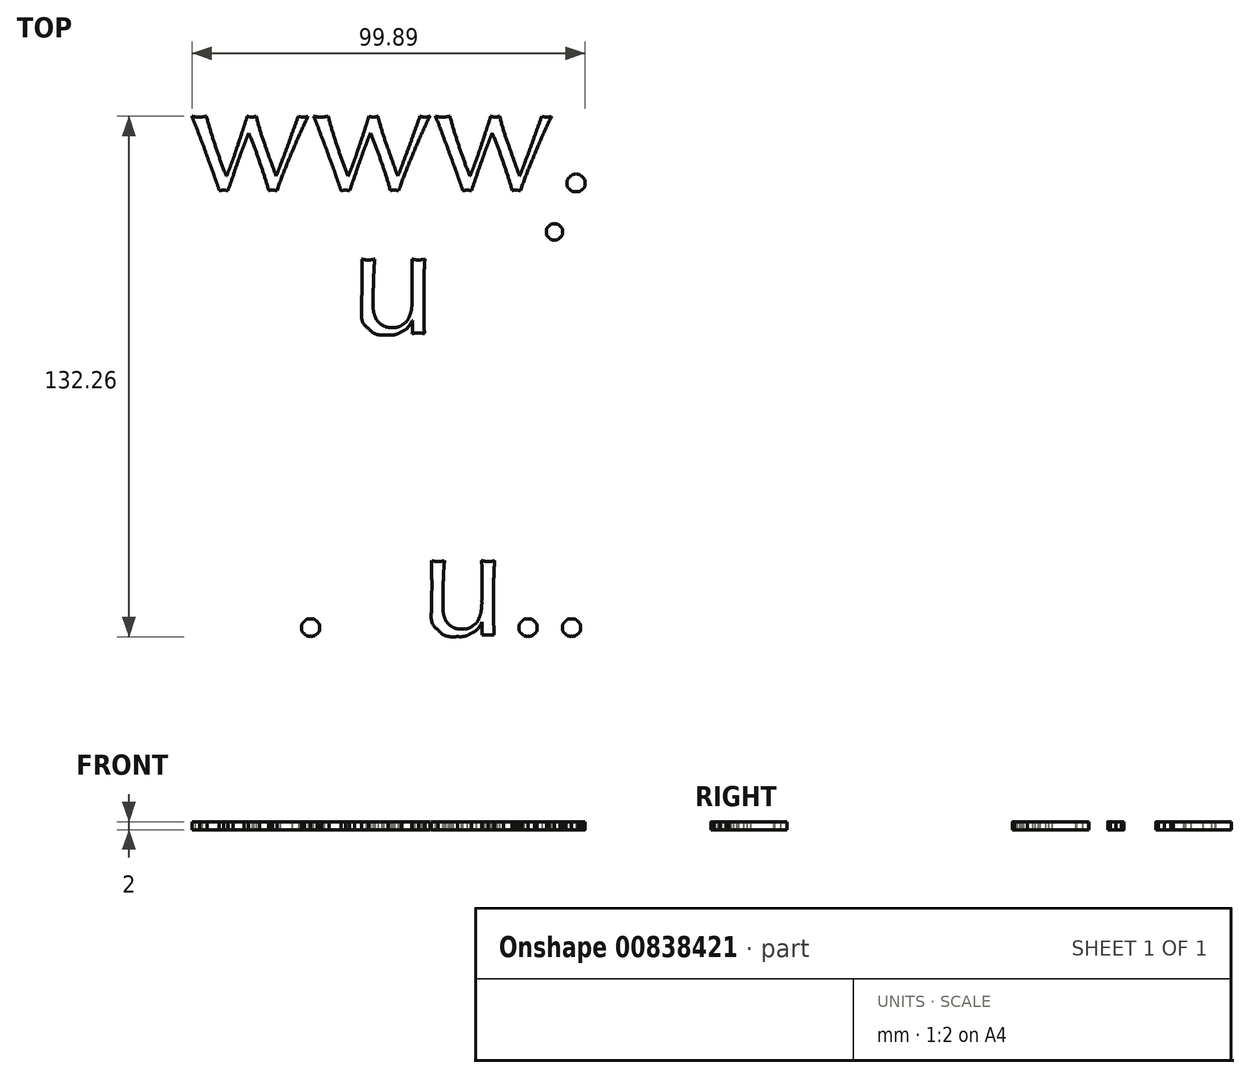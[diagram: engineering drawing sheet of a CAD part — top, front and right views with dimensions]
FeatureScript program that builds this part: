
annotation { "Feature Type Name" : "Feature", "Feature Type Description" : "" }
export const myFeature = defineFeature(function(context is Context, id is Id, definition is map)
    precondition{}
    {
        {
            var Q0;
            Q0=qCreatedBy(makeId("Top.planeOp"),FACE);
            var sketch = newSketch(context, id + "F0", { "sketchPlane" : qUnion([Q0])});
            skLineSegment(sketch, "E0", {"start": v(54.7, 60.68) * mm, "end": v(54.7, 58.25) * mm});
            skLineSegment(sketch, "E1", {"start": v(54.7, 58.25) * mm, "end": v(54.7, 60.68) * mm});
            skLineSegment(sketch, "E2", {"start": v(57.65, 51.93) * mm, "end": v(57.65, 54.51) * mm});
            skLineSegment(sketch, "E3", {"start": v(57.65, 54.51) * mm, "end": v(57.65, 51.93) * mm});
            skLineSegment(sketch, "E4", {"start": v(45.08, 65.22) * mm, "end": v(45, 65.22) * mm});
            skLineSegment(sketch, "E5", {"start": v(45, 65.22) * mm, "end": v(45.08, 65.22) * mm});
            skLineSegment(sketch, "E6", {"start": v(42.06, 60.96) * mm, "end": v(42.06, 56.82) * mm});
            skLineSegment(sketch, "E7", {"start": v(42.06, 56.82) * mm, "end": v(42.06, 60.96) * mm});
            skLineSegment(sketch, "E8", {"start": v(45, 56.82) * mm, "end": v(45, 60.2) * mm});
            skLineSegment(sketch, "E9", {"start": v(45, 60.2) * mm, "end": v(45, 56.82) * mm});
            skLineSegment(sketch, "E10", {"start": v(-41.95, 23.11) * mm, "end": v(-42.11, 17.14) * mm});
            skLineSegment(sketch, "E11", {"start": v(-42.11, 17.14) * mm, "end": v(-41.95, 23.11) * mm});
            skLineSegment(sketch, "E12", {"start": v(-51.78, 30.2) * mm, "end": v(-51.78, 28.12) * mm});
            skLineSegment(sketch, "E13", {"start": v(-51.78, 28.12) * mm, "end": v(-51.34, 28.12) * mm});
            skLineSegment(sketch, "E14", {"start": v(-51.34, 28.12) * mm, "end": v(-51.78, 30.2) * mm});
            skLineSegment(sketch, "E15", {"start": v(-36.7, 13.68) * mm, "end": v(-36.7, 14.56) * mm});
            skLineSegment(sketch, "E16", {"start": v(-36.7, 14.56) * mm, "end": v(-36.7, 13.68) * mm});
            skLineSegment(sketch, "E17", {"start": v(-28.94, 37.43) * mm, "end": v(-32.24, 36.04) * mm});
            skLineSegment(sketch, "E18", {"start": v(-32.24, 36.04) * mm, "end": v(-28.94, 37.43) * mm});
            skLineSegment(sketch, "E19", {"start": v(-33.28, 30.07) * mm, "end": v(-32, 30.07) * mm});
            skLineSegment(sketch, "E20", {"start": v(-32, 30.07) * mm, "end": v(-33.28, 30.07) * mm});
            skLineSegment(sketch, "E21", {"start": v(-24.33, 13.28) * mm, "end": v(-24.33, 14.24) * mm});
            skLineSegment(sketch, "E22", {"start": v(-24.33, 14.24) * mm, "end": v(-24.33, 13.28) * mm});
            skLineSegment(sketch, "E23", {"start": v(-29.06, 30.07) * mm, "end": v(-27.11, 30.07) * mm});
            skLineSegment(sketch, "E24", {"start": v(-27.11, 30.07) * mm, "end": v(-29.06, 30.07) * mm});
            skLineSegment(sketch, "E25", {"start": v(-24.88, 30.4) * mm, "end": v(-24.88, 30.83) * mm});
            skLineSegment(sketch, "E26", {"start": v(-24.88, 30.83) * mm, "end": v(-24.88, 31.23) * mm});
            skLineSegment(sketch, "E27", {"start": v(-24.88, 31.23) * mm, "end": v(-24.88, 30.4) * mm});
            skLineSegment(sketch, "E28", {"start": v(-28.74, 37.43) * mm, "end": v(-28.94, 37.43) * mm});
            skLineSegment(sketch, "E29", {"start": v(-28.94, 37.43) * mm, "end": v(-28.74, 37.43) * mm});
            skLineSegment(sketch, "E30", {"start": v(-8.4, 16.5) * mm, "end": v(-8.32, 16.5) * mm});
            skLineSegment(sketch, "E31", {"start": v(-8.32, 16.5) * mm, "end": v(-8.32, 14.8) * mm});
            skLineSegment(sketch, "E32", {"start": v(-8.32, 14.8) * mm, "end": v(-8.4, 16.5) * mm});
            skLineSegment(sketch, "E33", {"start": v(-8.4, 28.92) * mm, "end": v(-8.4, 25.58) * mm});
            skLineSegment(sketch, "E34", {"start": v(-8.4, 25.58) * mm, "end": v(-8.4, 28.92) * mm});
            skLineSegment(sketch, "E35", {"start": v(9.93, 28.84) * mm, "end": v(10.2, 29.04) * mm});
            skLineSegment(sketch, "E36", {"start": v(10.2, 29.04) * mm, "end": v(9.93, 28.84) * mm});
            skLineSegment(sketch, "E37", {"start": v(3.96, 28.2) * mm, "end": v(3.88, 28.24) * mm});
            skLineSegment(sketch, "E38", {"start": v(3.88, 28.24) * mm, "end": v(3.96, 28.2) * mm});
            skLineSegment(sketch, "E39", {"start": v(0.98, 23.87) * mm, "end": v(0.98, 22.6) * mm});
            skLineSegment(sketch, "E40", {"start": v(0.98, 22.6) * mm, "end": v(0.98, 23.87) * mm});
            skLineSegment(sketch, "E41", {"start": v(3.92, 19.57) * mm, "end": v(3.92, 23.95) * mm});
            skLineSegment(sketch, "E42", {"start": v(3.92, 23.95) * mm, "end": v(3.92, 19.57) * mm});
            skLineSegment(sketch, "E43", {"start": v(15.14, 31.74) * mm, "end": v(15.14, 24.54) * mm});
            skLineSegment(sketch, "E44", {"start": v(15.14, 24.54) * mm, "end": v(15.14, 31.74) * mm});
            skLineSegment(sketch, "E45", {"start": v(18.09, 24.54) * mm, "end": v(18.09, 31.74) * mm});
            skLineSegment(sketch, "E46", {"start": v(18.09, 31.74) * mm, "end": v(18.09, 24.54) * mm});
            skLineSegment(sketch, "E47", {"start": v(26.26, 24.66) * mm, "end": v(26.26, 20.52) * mm});
            skLineSegment(sketch, "E48", {"start": v(26.26, 20.52) * mm, "end": v(26.26, 24.66) * mm});
            skLineSegment(sketch, "E49", {"start": v(29.2, 20.52) * mm, "end": v(29.2, 24.66) * mm});
            skLineSegment(sketch, "E50", {"start": v(29.2, 24.66) * mm, "end": v(29.2, 20.52) * mm});
            skLineSegment(sketch, "E51", {"start": v(39.12, 20.13) * mm, "end": v(39.12, 20.05) * mm});
            skLineSegment(sketch, "E52", {"start": v(39.12, 20.05) * mm, "end": v(39.12, 20.13) * mm});
            skLineSegment(sketch, "E53", {"start": v(38.8, 13.56) * mm, "end": v(38.8, 13.48) * mm});
            skLineSegment(sketch, "E54", {"start": v(38.8, 13.48) * mm, "end": v(38.8, 13.56) * mm});
            skLineSegment(sketch, "E55", {"start": v(47.56, 30.95) * mm, "end": v(47.64, 31.03) * mm});
            skLineSegment(sketch, "E56", {"start": v(47.64, 31.03) * mm, "end": v(47.56, 30.95) * mm});
            skLineSegment(sketch, "E57", {"start": v(-44.7, -11.51) * mm, "end": v(-44.79, -11.51) * mm});
            skLineSegment(sketch, "E58", {"start": v(-44.79, -11.51) * mm, "end": v(-44.7, -11.51) * mm});
            skLineSegment(sketch, "E59", {"start": v(-47.73, -8.13) * mm, "end": v(-47.73, -15.33) * mm});
            skLineSegment(sketch, "E60", {"start": v(-47.73, -15.33) * mm, "end": v(-47.73, -8.13) * mm});
            skLineSegment(sketch, "E61", {"start": v(-48.05, -26.6) * mm, "end": v(-47.33, -26.6) * mm});
            skLineSegment(sketch, "E62", {"start": v(-47.33, -26.6) * mm, "end": v(-48.05, -26.6) * mm});
            skLineSegment(sketch, "E63", {"start": v(-14.92, -16.77) * mm, "end": v(-15.08, -22.73) * mm});
            skLineSegment(sketch, "E64", {"start": v(-15.08, -22.73) * mm, "end": v(-14.92, -16.77) * mm});
            skLineSegment(sketch, "E65", {"start": v(-24.75, -9.68) * mm, "end": v(-24.75, -11.75) * mm});
            skLineSegment(sketch, "E66", {"start": v(-24.75, -11.75) * mm, "end": v(-24.31, -11.75) * mm});
            skLineSegment(sketch, "E67", {"start": v(-24.31, -11.75) * mm, "end": v(-24.75, -9.68) * mm});
            skLineSegment(sketch, "E68", {"start": v(-9.67, -26.2) * mm, "end": v(-9.67, -25.32) * mm});
            skLineSegment(sketch, "E69", {"start": v(-9.67, -25.32) * mm, "end": v(-9.67, -26.2) * mm});
            skLineSegment(sketch, "E70", {"start": v(-4.3, -8.13) * mm, "end": v(-4.3, -15.33) * mm});
            skLineSegment(sketch, "E71", {"start": v(-4.3, -15.33) * mm, "end": v(-4.3, -8.13) * mm});
            skLineSegment(sketch, "E72", {"start": v(-1.35, -15.33) * mm, "end": v(-1.35, -8.13) * mm});
            skLineSegment(sketch, "E73", {"start": v(-1.35, -8.13) * mm, "end": v(-1.35, -15.33) * mm});
            skLineSegment(sketch, "E74", {"start": v(16, -16.77) * mm, "end": v(15.85, -22.73) * mm});
            skLineSegment(sketch, "E75", {"start": v(15.85, -22.73) * mm, "end": v(16, -16.77) * mm});
            skLineSegment(sketch, "E76", {"start": v(6.18, -9.68) * mm, "end": v(6.18, -11.75) * mm});
            skLineSegment(sketch, "E77", {"start": v(6.18, -11.75) * mm, "end": v(6.62, -11.75) * mm});
            skLineSegment(sketch, "E78", {"start": v(6.62, -11.75) * mm, "end": v(6.18, -9.68) * mm});
            skLineSegment(sketch, "E79", {"start": v(21.26, -26.2) * mm, "end": v(21.26, -25.32) * mm});
            skLineSegment(sketch, "E80", {"start": v(21.26, -25.32) * mm, "end": v(21.26, -26.2) * mm});
            skLineSegment(sketch, "E81", {"start": v(38.57, -15.5) * mm, "end": v(38.57, -17.92) * mm});
            skLineSegment(sketch, "E82", {"start": v(38.57, -17.92) * mm, "end": v(38.57, -15.5) * mm});
            skLineSegment(sketch, "E83", {"start": v(41.51, -24.25) * mm, "end": v(41.51, -21.66) * mm});
            skLineSegment(sketch, "E84", {"start": v(41.51, -21.66) * mm, "end": v(41.51, -24.25) * mm});
            skLineSegment(sketch, "E85", {"start": v(28.94, -10.96) * mm, "end": v(28.86, -10.96) * mm});
            skLineSegment(sketch, "E86", {"start": v(28.86, -10.96) * mm, "end": v(28.94, -10.96) * mm});
            skLineSegment(sketch, "E87", {"start": v(25.92, -15.21) * mm, "end": v(25.92, -19.35) * mm});
            skLineSegment(sketch, "E88", {"start": v(25.92, -19.35) * mm, "end": v(25.92, -15.21) * mm});
            skLineSegment(sketch, "E89", {"start": v(28.86, -19.35) * mm, "end": v(28.86, -15.97) * mm});
            skLineSegment(sketch, "E90", {"start": v(28.86, -15.97) * mm, "end": v(28.86, -19.35) * mm});
            skLineSegment(sketch, "E91", {"start": v(-52.39, -59.72) * mm, "end": v(-52.86, -59.72) * mm});
            skLineSegment(sketch, "E92", {"start": v(-52.86, -59.72) * mm, "end": v(-52.39, -59.72) * mm});
            skLineSegment(sketch, "E93", {"start": v(-43.83, -48.06) * mm, "end": v(-43.35, -48.06) * mm});
            skLineSegment(sketch, "E94", {"start": v(-43.35, -48.06) * mm, "end": v(-43.83, -48.06) * mm});
            skLineSegment(sketch, "E95", {"start": v(-12.72, -52.24) * mm, "end": v(-12.72, -54.67) * mm});
            skLineSegment(sketch, "E96", {"start": v(-12.72, -54.67) * mm, "end": v(-12.72, -52.24) * mm});
            skLineSegment(sketch, "E97", {"start": v(-9.77, -61) * mm, "end": v(-9.77, -58.4) * mm});
            skLineSegment(sketch, "E98", {"start": v(-9.77, -58.4) * mm, "end": v(-9.77, -61) * mm});
            skLineSegment(sketch, "E99", {"start": v(-22.35, -47.7) * mm, "end": v(-22.42, -47.7) * mm});
            skLineSegment(sketch, "E100", {"start": v(-22.42, -47.7) * mm, "end": v(-22.35, -47.7) * mm});
            skLineSegment(sketch, "E101", {"start": v(-25.37, -51.96) * mm, "end": v(-25.37, -56.1) * mm});
            skLineSegment(sketch, "E102", {"start": v(-25.37, -56.1) * mm, "end": v(-25.37, -51.96) * mm});
            skLineSegment(sketch, "E103", {"start": v(-22.42, -56.1) * mm, "end": v(-22.42, -52.72) * mm});
            skLineSegment(sketch, "E104", {"start": v(-22.42, -52.72) * mm, "end": v(-22.42, -56.1) * mm});
            skLineSegment(sketch, "E105", {"start": v(9.31, -60.12) * mm, "end": v(9.4, -60.12) * mm});
            skLineSegment(sketch, "E106", {"start": v(9.4, -60.12) * mm, "end": v(9.4, -61.83) * mm});
            skLineSegment(sketch, "E107", {"start": v(9.4, -61.83) * mm, "end": v(9.31, -60.12) * mm});
            skLineSegment(sketch, "E108", {"start": v(9.31, -47.7) * mm, "end": v(9.31, -51.05) * mm});
            skLineSegment(sketch, "E109", {"start": v(9.31, -51.05) * mm, "end": v(9.31, -47.7) * mm});
            skLineSegment(sketch, "E110", {"start": v(41.63, -44.88) * mm, "end": v(41.63, -52.08) * mm});
            skLineSegment(sketch, "E111", {"start": v(41.63, -52.08) * mm, "end": v(41.63, -44.88) * mm});
            skLineSegment(sketch, "E112", {"start": v(44.58, -52.08) * mm, "end": v(44.58, -44.88) * mm});
            skLineSegment(sketch, "E113", {"start": v(44.58, -44.88) * mm, "end": v(44.58, -52.08) * mm});
            skLineSegment(sketch, "E114", {"start": v(52.75, -44.88) * mm, "end": v(52.75, -52.08) * mm});
            skLineSegment(sketch, "E115", {"start": v(52.75, -52.08) * mm, "end": v(52.75, -44.88) * mm});
            skLineSegment(sketch, "E116", {"start": v(55.7, -52.08) * mm, "end": v(55.7, -44.88) * mm});
            skLineSegment(sketch, "E117", {"start": v(55.7, -44.88) * mm, "end": v(55.7, -52.08) * mm});
            skFitSpline(sketch, "E118", {"points": [v(-57.43, 49.5) * mm, v(-57.1, 49.55) * mm, v(-56.74, 49.58) * mm, v(-56.31, 49.58) * mm]});
            skFitSpline(sketch, "E119", {"points": [v(-56.31, 49.58) * mm, v(-55.89, 49.58) * mm, v(-55.52, 49.55) * mm, v(-55.2, 49.5) * mm]});
            skFitSpline(sketch, "E120", {"points": [v(-55.2, 49.5) * mm, v(-54.83, 50.62) * mm, v(-54.4, 51.86) * mm, v(-53.93, 53.24) * mm]});
            skFitSpline(sketch, "E121", {"points": [v(-53.93, 53.24) * mm, v(-53.45, 54.65) * mm, v(-52.97, 56.03) * mm, v(-52.5, 57.38) * mm]});
            skFitSpline(sketch, "E122", {"points": [v(-52.5, 57.38) * mm, v(-52.02, 58.73) * mm, v(-51.55, 60) * mm, v(-51.1, 61.16) * mm]});
            skFitSpline(sketch, "E123", {"points": [v(-51.1, 61.16) * mm, v(-50.65, 62.35) * mm, v(-50.27, 63.35) * mm, v(-49.95, 64.14) * mm]});
            skFitSpline(sketch, "E124", {"points": [v(-49.95, 64.14) * mm, v(-48.89, 61.52) * mm, v(-47.94, 59.01) * mm, v(-47.12, 56.62) * mm]});
            skFitSpline(sketch, "E125", {"points": [v(-47.12, 56.62) * mm, v(-46.3, 54.24) * mm, v(-45.54, 51.86) * mm, v(-44.85, 49.5) * mm]});
            skFitSpline(sketch, "E126", {"points": [v(-44.85, 49.5) * mm, v(-44.72, 49.55) * mm, v(-44.56, 49.58) * mm, v(-44.38, 49.58) * mm]});
            skFitSpline(sketch, "E127", {"points": [v(-44.38, 49.58) * mm, v(-44.2, 49.58) * mm, v(-44, 49.58) * mm, v(-43.82, 49.58) * mm]});
            skFitSpline(sketch, "E128", {"points": [v(-43.82, 49.58) * mm, v(-43.42, 49.58) * mm, v(-43.08, 49.55) * mm, v(-42.79, 49.5) * mm]});
            skFitSpline(sketch, "E129", {"points": [v(-42.79, 49.5) * mm, v(-41.64, 52.63) * mm, v(-40.42, 55.76) * mm, v(-39.12, 58.9) * mm]});
            skFitSpline(sketch, "E130", {"points": [v(-39.12, 58.9) * mm, v(-37.8, 62.02) * mm, v(-36.38, 65.2) * mm, v(-34.87, 68.4) * mm]});
            skFitSpline(sketch, "E131", {"points": [v(-34.87, 68.4) * mm, v(-35.32, 68.27) * mm, v(-35.72, 68.2) * mm, v(-36.06, 68.2) * mm]});
            skFitSpline(sketch, "E132", {"points": [v(-36.06, 68.2) * mm, v(-36.38, 68.2) * mm, v(-36.8, 68.27) * mm, v(-37.33, 68.4) * mm]});
            skFitSpline(sketch, "E133", {"points": [v(-37.33, 68.4) * mm, v(-37.79, 67.15) * mm, v(-38.28, 65.81) * mm, v(-38.8, 64.38) * mm]});
            skFitSpline(sketch, "E134", {"points": [v(-38.8, 64.38) * mm, v(-39.31, 62.95) * mm, v(-39.81, 61.54) * mm, v(-40.32, 60.16) * mm]});
            skFitSpline(sketch, "E135", {"points": [v(-40.32, 60.16) * mm, v(-40.82, 58.81) * mm, v(-41.31, 57.51) * mm, v(-41.8, 56.27) * mm]});
            skFitSpline(sketch, "E136", {"points": [v(-41.8, 56.27) * mm, v(-42.24, 55.05) * mm, v(-42.64, 54.01) * mm, v(-42.98, 53.16) * mm]});
            skFitSpline(sketch, "E137", {"points": [v(-42.98, 53.16) * mm, v(-43.94, 55.81) * mm, v(-44.85, 58.37) * mm, v(-45.73, 60.84) * mm]});
            skFitSpline(sketch, "E138", {"points": [v(-45.73, 60.84) * mm, v(-46.6, 63.33) * mm, v(-47.37, 65.85) * mm, v(-48.04, 68.4) * mm]});
            skFitSpline(sketch, "E139", {"points": [v(-48.04, 68.4) * mm, v(-48.25, 68.35) * mm, v(-48.43, 68.3) * mm, v(-48.6, 68.24) * mm]});
            skFitSpline(sketch, "E140", {"points": [v(-48.6, 68.24) * mm, v(-48.75, 68.22) * mm, v(-48.94, 68.2) * mm, v(-49.15, 68.2) * mm]});
            skFitSpline(sketch, "E141", {"points": [v(-49.15, 68.2) * mm, v(-49.47, 68.2) * mm, v(-49.87, 68.27) * mm, v(-50.34, 68.4) * mm]});
            skFitSpline(sketch, "E142", {"points": [v(-50.34, 68.4) * mm, v(-50.72, 67.15) * mm, v(-51.14, 65.8) * mm, v(-51.62, 64.34) * mm]});
            skFitSpline(sketch, "E143", {"points": [v(-51.62, 64.34) * mm, v(-52.1, 62.88) * mm, v(-52.57, 61.45) * mm, v(-53.05, 60.05) * mm]});
            skFitSpline(sketch, "E144", {"points": [v(-53.05, 60.05) * mm, v(-53.53, 58.64) * mm, v(-54, 57.33) * mm, v(-54.44, 56.1) * mm]});
            skFitSpline(sketch, "E145", {"points": [v(-54.44, 56.1) * mm, v(-54.9, 54.89) * mm, v(-55.28, 53.9) * mm, v(-55.6, 53.16) * mm]});
            skFitSpline(sketch, "E146", {"points": [v(-55.6, 53.16) * mm, v(-56.63, 55.81) * mm, v(-57.57, 58.39) * mm, v(-58.42, 60.88) * mm]});
            skFitSpline(sketch, "E147", {"points": [v(-58.42, 60.88) * mm, v(-59.24, 63.4) * mm, v(-60, 65.9) * mm, v(-60.69, 68.4) * mm]});
            skFitSpline(sketch, "E148", {"points": [v(-60.69, 68.4) * mm, v(-61.03, 68.35) * mm, v(-61.35, 68.3) * mm, v(-61.64, 68.24) * mm]});
            skFitSpline(sketch, "E149", {"points": [v(-61.64, 68.24) * mm, v(-61.94, 68.22) * mm, v(-62.23, 68.2) * mm, v(-62.52, 68.2) * mm]});
            skFitSpline(sketch, "E150", {"points": [v(-62.52, 68.2) * mm, v(-62.84, 68.2) * mm, v(-63.16, 68.22) * mm, v(-63.47, 68.24) * mm]});
            skFitSpline(sketch, "E151", {"points": [v(-63.47, 68.24) * mm, v(-63.77, 68.3) * mm, v(-64.07, 68.35) * mm, v(-64.39, 68.4) * mm]});
            skFitSpline(sketch, "E152", {"points": [v(-64.39, 68.4) * mm, v(-63.73, 66.8) * mm, v(-63.06, 65.11) * mm, v(-62.4, 63.3) * mm]});
            skFitSpline(sketch, "E153", {"points": [v(-62.4, 63.3) * mm, v(-61.71, 61.53) * mm, v(-61.06, 59.78) * mm, v(-60.45, 58.06) * mm]});
            skFitSpline(sketch, "E154", {"points": [v(-60.45, 58.06) * mm, v(-59.81, 56.36) * mm, v(-59.23, 54.75) * mm, v(-58.7, 53.24) * mm]});
            skFitSpline(sketch, "E155", {"points": [v(-58.7, 53.24) * mm, v(-58.17, 51.73) * mm, v(-57.75, 50.48) * mm, v(-57.43, 49.5) * mm]});
            skFitSpline(sketch, "E156", {"points": [v(-26.5, 49.5) * mm, v(-26.18, 49.55) * mm, v(-25.8, 49.58) * mm, v(-25.38, 49.58) * mm]});
            skFitSpline(sketch, "E157", {"points": [v(-25.38, 49.58) * mm, v(-24.96, 49.58) * mm, v(-24.59, 49.55) * mm, v(-24.27, 49.5) * mm]});
            skFitSpline(sketch, "E158", {"points": [v(-24.27, 49.5) * mm, v(-23.9, 50.62) * mm, v(-23.47, 51.86) * mm, v(-23, 53.24) * mm]});
            skFitSpline(sketch, "E159", {"points": [v(-23, 53.24) * mm, v(-22.52, 54.65) * mm, v(-22.04, 56.03) * mm, v(-21.56, 57.38) * mm]});
            skFitSpline(sketch, "E160", {"points": [v(-21.56, 57.38) * mm, v(-21.09, 58.73) * mm, v(-20.62, 60) * mm, v(-20.17, 61.16) * mm]});
            skFitSpline(sketch, "E161", {"points": [v(-20.17, 61.16) * mm, v(-19.72, 62.35) * mm, v(-19.34, 63.35) * mm, v(-19.02, 64.14) * mm]});
            skFitSpline(sketch, "E162", {"points": [v(-19.02, 64.14) * mm, v(-17.96, 61.52) * mm, v(-17.02, 59.01) * mm, v(-16.2, 56.62) * mm]});
            skFitSpline(sketch, "E163", {"points": [v(-16.2, 56.62) * mm, v(-15.37, 54.24) * mm, v(-14.61, 51.86) * mm, v(-13.93, 49.5) * mm]});
            skFitSpline(sketch, "E164", {"points": [v(-13.93, 49.5) * mm, v(-13.8, 49.55) * mm, v(-13.63, 49.58) * mm, v(-13.45, 49.58) * mm]});
            skFitSpline(sketch, "E165", {"points": [v(-13.45, 49.58) * mm, v(-13.26, 49.58) * mm, v(-13.08, 49.58) * mm, v(-12.9, 49.58) * mm]});
            skFitSpline(sketch, "E166", {"points": [v(-12.9, 49.58) * mm, v(-12.5, 49.58) * mm, v(-12.15, 49.55) * mm, v(-11.86, 49.5) * mm]});
            skFitSpline(sketch, "E167", {"points": [v(-11.86, 49.5) * mm, v(-10.72, 52.63) * mm, v(-9.5, 55.76) * mm, v(-8.2, 58.9) * mm]});
            skFitSpline(sketch, "E168", {"points": [v(-8.2, 58.9) * mm, v(-6.87, 62.02) * mm, v(-5.45, 65.2) * mm, v(-3.94, 68.4) * mm]});
            skFitSpline(sketch, "E169", {"points": [v(-3.94, 68.4) * mm, v(-4.39, 68.27) * mm, v(-4.79, 68.2) * mm, v(-5.13, 68.2) * mm]});
            skFitSpline(sketch, "E170", {"points": [v(-5.13, 68.2) * mm, v(-5.45, 68.2) * mm, v(-5.87, 68.27) * mm, v(-6.4, 68.4) * mm]});
            skFitSpline(sketch, "E171", {"points": [v(-6.4, 68.4) * mm, v(-6.86, 67.15) * mm, v(-7.35, 65.81) * mm, v(-7.88, 64.38) * mm]});
            skFitSpline(sketch, "E172", {"points": [v(-7.88, 64.38) * mm, v(-8.38, 62.95) * mm, v(-8.89, 61.54) * mm, v(-9.39, 60.16) * mm]});
            skFitSpline(sketch, "E173", {"points": [v(-9.39, 60.16) * mm, v(-9.9, 58.81) * mm, v(-10.38, 57.51) * mm, v(-10.86, 56.27) * mm]});
            skFitSpline(sketch, "E174", {"points": [v(-10.86, 56.27) * mm, v(-11.31, 55.05) * mm, v(-11.71, 54.01) * mm, v(-12.06, 53.16) * mm]});
            skFitSpline(sketch, "E175", {"points": [v(-12.06, 53.16) * mm, v(-13.01, 55.81) * mm, v(-13.93, 58.37) * mm, v(-14.8, 60.84) * mm]});
            skFitSpline(sketch, "E176", {"points": [v(-14.8, 60.84) * mm, v(-15.68, 63.33) * mm, v(-16.45, 65.85) * mm, v(-17.1, 68.4) * mm]});
            skFitSpline(sketch, "E177", {"points": [v(-17.1, 68.4) * mm, v(-17.32, 68.35) * mm, v(-17.5, 68.3) * mm, v(-17.67, 68.24) * mm]});
            skFitSpline(sketch, "E178", {"points": [v(-17.67, 68.24) * mm, v(-17.82, 68.22) * mm, v(-18.01, 68.2) * mm, v(-18.22, 68.2) * mm]});
            skFitSpline(sketch, "E179", {"points": [v(-18.22, 68.2) * mm, v(-18.54, 68.2) * mm, v(-18.94, 68.27) * mm, v(-19.42, 68.4) * mm]});
            skFitSpline(sketch, "E180", {"points": [v(-19.42, 68.4) * mm, v(-19.79, 67.15) * mm, v(-20.21, 65.8) * mm, v(-20.69, 64.34) * mm]});
            skFitSpline(sketch, "E181", {"points": [v(-20.69, 64.34) * mm, v(-21.17, 62.88) * mm, v(-21.64, 61.45) * mm, v(-22.12, 60.05) * mm]});
            skFitSpline(sketch, "E182", {"points": [v(-22.12, 60.05) * mm, v(-22.6, 58.64) * mm, v(-23.06, 57.33) * mm, v(-23.51, 56.1) * mm]});
            skFitSpline(sketch, "E183", {"points": [v(-23.51, 56.1) * mm, v(-23.97, 54.89) * mm, v(-24.35, 53.9) * mm, v(-24.67, 53.16) * mm]});
            skFitSpline(sketch, "E184", {"points": [v(-24.67, 53.16) * mm, v(-25.7, 55.81) * mm, v(-26.64, 58.39) * mm, v(-27.5, 60.88) * mm]});
            skFitSpline(sketch, "E185", {"points": [v(-27.5, 60.88) * mm, v(-28.32, 63.4) * mm, v(-29.07, 65.9) * mm, v(-29.76, 68.4) * mm]});
            skFitSpline(sketch, "E186", {"points": [v(-29.76, 68.4) * mm, v(-30.1, 68.35) * mm, v(-30.42, 68.3) * mm, v(-30.72, 68.24) * mm]});
            skFitSpline(sketch, "E187", {"points": [v(-30.72, 68.24) * mm, v(-31, 68.22) * mm, v(-31.3, 68.2) * mm, v(-31.6, 68.2) * mm]});
            skFitSpline(sketch, "E188", {"points": [v(-31.6, 68.2) * mm, v(-31.9, 68.2) * mm, v(-32.23, 68.22) * mm, v(-32.55, 68.24) * mm]});
            skFitSpline(sketch, "E189", {"points": [v(-32.55, 68.24) * mm, v(-32.84, 68.3) * mm, v(-33.14, 68.35) * mm, v(-33.46, 68.4) * mm]});
            skFitSpline(sketch, "E190", {"points": [v(-33.46, 68.4) * mm, v(-32.8, 66.8) * mm, v(-32.13, 65.11) * mm, v(-31.47, 63.3) * mm]});
            skFitSpline(sketch, "E191", {"points": [v(-31.47, 63.3) * mm, v(-30.78, 61.53) * mm, v(-30.13, 59.78) * mm, v(-29.52, 58.06) * mm]});
            skFitSpline(sketch, "E192", {"points": [v(-29.52, 58.06) * mm, v(-28.89, 56.36) * mm, v(-28.3, 54.75) * mm, v(-27.77, 53.24) * mm]});
            skFitSpline(sketch, "E193", {"points": [v(-27.77, 53.24) * mm, v(-27.24, 51.73) * mm, v(-26.82, 50.48) * mm, v(-26.5, 49.5) * mm]});
            skFitSpline(sketch, "E194", {"points": [v(4.43, 49.5) * mm, v(4.75, 49.55) * mm, v(5.12, 49.58) * mm, v(5.54, 49.58) * mm]});
            skFitSpline(sketch, "E195", {"points": [v(5.54, 49.58) * mm, v(5.97, 49.58) * mm, v(6.34, 49.55) * mm, v(6.66, 49.5) * mm]});
            skFitSpline(sketch, "E196", {"points": [v(6.66, 49.5) * mm, v(7.03, 50.62) * mm, v(7.45, 51.86) * mm, v(7.93, 53.24) * mm]});
            skFitSpline(sketch, "E197", {"points": [v(7.93, 53.24) * mm, v(8.4, 54.65) * mm, v(8.89, 56.03) * mm, v(9.36, 57.38) * mm]});
            skFitSpline(sketch, "E198", {"points": [v(9.36, 57.38) * mm, v(9.84, 58.73) * mm, v(10.3, 60) * mm, v(10.76, 61.16) * mm]});
            skFitSpline(sketch, "E199", {"points": [v(10.76, 61.16) * mm, v(11.2, 62.35) * mm, v(11.6, 63.35) * mm, v(11.91, 64.14) * mm]});
            skFitSpline(sketch, "E200", {"points": [v(11.91, 64.14) * mm, v(12.97, 61.52) * mm, v(13.91, 59.01) * mm, v(14.74, 56.62) * mm]});
            skFitSpline(sketch, "E201", {"points": [v(14.74, 56.62) * mm, v(15.56, 54.24) * mm, v(16.31, 51.86) * mm, v(17, 49.5) * mm]});
            skFitSpline(sketch, "E202", {"points": [v(17, 49.5) * mm, v(17.14, 49.55) * mm, v(17.3, 49.58) * mm, v(17.48, 49.58) * mm]});
            skFitSpline(sketch, "E203", {"points": [v(17.48, 49.58) * mm, v(17.67, 49.58) * mm, v(17.85, 49.58) * mm, v(18.04, 49.58) * mm]});
            skFitSpline(sketch, "E204", {"points": [v(18.04, 49.58) * mm, v(18.44, 49.58) * mm, v(18.78, 49.55) * mm, v(19.07, 49.5) * mm]});
            skFitSpline(sketch, "E205", {"points": [v(19.07, 49.5) * mm, v(20.21, 52.63) * mm, v(21.43, 55.76) * mm, v(22.73, 58.9) * mm]});
            skFitSpline(sketch, "E206", {"points": [v(22.73, 58.9) * mm, v(24.06, 62.02) * mm, v(25.48, 65.2) * mm, v(27, 68.4) * mm]});
            skFitSpline(sketch, "E207", {"points": [v(27, 68.4) * mm, v(26.54, 68.27) * mm, v(26.14, 68.2) * mm, v(25.8, 68.2) * mm]});
            skFitSpline(sketch, "E208", {"points": [v(25.8, 68.2) * mm, v(25.48, 68.2) * mm, v(25.05, 68.27) * mm, v(24.52, 68.4) * mm]});
            skFitSpline(sketch, "E209", {"points": [v(24.52, 68.4) * mm, v(24.07, 67.15) * mm, v(23.58, 65.81) * mm, v(23.05, 64.38) * mm]});
            skFitSpline(sketch, "E210", {"points": [v(23.05, 64.38) * mm, v(22.55, 62.95) * mm, v(22.04, 61.54) * mm, v(21.54, 60.16) * mm]});
            skFitSpline(sketch, "E211", {"points": [v(21.54, 60.16) * mm, v(21.04, 58.81) * mm, v(20.54, 57.51) * mm, v(20.07, 56.27) * mm]});
            skFitSpline(sketch, "E212", {"points": [v(20.07, 56.27) * mm, v(19.62, 55.05) * mm, v(19.22, 54.01) * mm, v(18.87, 53.16) * mm]});
            skFitSpline(sketch, "E213", {"points": [v(18.87, 53.16) * mm, v(17.92, 55.81) * mm, v(17, 58.37) * mm, v(16.13, 60.84) * mm]});
            skFitSpline(sketch, "E214", {"points": [v(16.13, 60.84) * mm, v(15.25, 63.33) * mm, v(14.48, 65.85) * mm, v(13.82, 68.4) * mm]});
            skFitSpline(sketch, "E215", {"points": [v(13.82, 68.4) * mm, v(13.6, 68.35) * mm, v(13.42, 68.3) * mm, v(13.26, 68.24) * mm]});
            skFitSpline(sketch, "E216", {"points": [v(13.26, 68.24) * mm, v(13.1, 68.22) * mm, v(12.92, 68.2) * mm, v(12.7, 68.2) * mm]});
            skFitSpline(sketch, "E217", {"points": [v(12.7, 68.2) * mm, v(12.39, 68.2) * mm, v(12, 68.27) * mm, v(11.51, 68.4) * mm]});
            skFitSpline(sketch, "E218", {"points": [v(11.51, 68.4) * mm, v(11.14, 67.15) * mm, v(10.72, 65.8) * mm, v(10.24, 64.34) * mm]});
            skFitSpline(sketch, "E219", {"points": [v(10.24, 64.34) * mm, v(9.76, 62.88) * mm, v(9.28, 61.45) * mm, v(8.8, 60.05) * mm]});
            skFitSpline(sketch, "E220", {"points": [v(8.8, 60.05) * mm, v(8.33, 58.64) * mm, v(7.87, 57.33) * mm, v(7.41, 56.1) * mm]});
            skFitSpline(sketch, "E221", {"points": [v(7.41, 56.1) * mm, v(6.96, 54.89) * mm, v(6.58, 53.9) * mm, v(6.26, 53.16) * mm]});
            skFitSpline(sketch, "E222", {"points": [v(6.26, 53.16) * mm, v(5.23, 55.81) * mm, v(4.28, 58.39) * mm, v(3.44, 60.88) * mm]});
            skFitSpline(sketch, "E223", {"points": [v(3.44, 60.88) * mm, v(2.61, 63.4) * mm, v(1.86, 65.9) * mm, v(1.17, 68.4) * mm]});
            skFitSpline(sketch, "E224", {"points": [v(1.17, 68.4) * mm, v(0.82, 68.35) * mm, v(0.5, 68.3) * mm, v(0.21, 68.24) * mm]});
            skFitSpline(sketch, "E225", {"points": [v(0.21, 68.24) * mm, v(-0.08, 68.22) * mm, v(-0.37, 68.2) * mm, v(-0.66, 68.2) * mm]});
            skFitSpline(sketch, "E226", {"points": [v(-0.66, 68.2) * mm, v(-0.98, 68.2) * mm, v(-1.3, 68.22) * mm, v(-1.62, 68.24) * mm]});
            skFitSpline(sketch, "E227", {"points": [v(-1.62, 68.24) * mm, v(-1.9, 68.3) * mm, v(-2.21, 68.35) * mm, v(-2.53, 68.4) * mm]});
            skFitSpline(sketch, "E228", {"points": [v(-2.53, 68.4) * mm, v(-1.87, 66.8) * mm, v(-1.2, 65.11) * mm, v(-0.54, 63.3) * mm]});
            skFitSpline(sketch, "E229", {"points": [v(-0.54, 63.3) * mm, v(0.15, 61.53) * mm, v(0.8, 59.78) * mm, v(1.4, 58.06) * mm]});
            skFitSpline(sketch, "E230", {"points": [v(1.4, 58.06) * mm, v(2.04, 56.36) * mm, v(2.63, 54.75) * mm, v(3.16, 53.24) * mm]});
            skFitSpline(sketch, "E231", {"points": [v(3.16, 53.24) * mm, v(3.69, 51.73) * mm, v(4.11, 50.48) * mm, v(4.43, 49.5) * mm]});
            skFitSpline(sketch, "E232", {"points": [v(30.94, 51.37) * mm, v(30.94, 50.76) * mm, v(31.17, 50.24) * mm, v(31.62, 49.82) * mm]});
            skFitSpline(sketch, "E233", {"points": [v(31.62, 49.82) * mm, v(32.07, 49.42) * mm, v(32.6, 49.22) * mm, v(33.21, 49.22) * mm]});
            skFitSpline(sketch, "E234", {"points": [v(33.21, 49.22) * mm, v(33.82, 49.22) * mm, v(34.35, 49.42) * mm, v(34.8, 49.82) * mm]});
            skFitSpline(sketch, "E235", {"points": [v(34.8, 49.82) * mm, v(35.25, 50.24) * mm, v(35.48, 50.76) * mm, v(35.48, 51.37) * mm]});
            skFitSpline(sketch, "E236", {"points": [v(35.48, 51.37) * mm, v(35.48, 51.98) * mm, v(35.25, 52.51) * mm, v(34.8, 52.96) * mm]});
            skFitSpline(sketch, "E237", {"points": [v(34.8, 52.96) * mm, v(34.35, 53.41) * mm, v(33.82, 53.64) * mm, v(33.21, 53.64) * mm]});
            skFitSpline(sketch, "E238", {"points": [v(33.21, 53.64) * mm, v(32.6, 53.64) * mm, v(32.07, 53.41) * mm, v(31.62, 52.96) * mm]});
            skFitSpline(sketch, "E239", {"points": [v(31.62, 52.96) * mm, v(31.17, 52.51) * mm, v(30.94, 51.98) * mm, v(30.94, 51.37) * mm]});
            skFitSpline(sketch, "E240", {"points": [v(54.7, 58.25) * mm, v(54.7, 56.72) * mm, v(54.67, 55.22) * mm, v(54.6, 53.76) * mm]});
            skFitSpline(sketch, "E241", {"points": [v(54.6, 53.76) * mm, v(54.54, 52.3) * mm, v(54.48, 50.88) * mm, v(54.43, 49.5) * mm]});
            skFitSpline(sketch, "E242", {"points": [v(54.43, 49.5) * mm, v(54.96, 49.55) * mm, v(55.5, 49.58) * mm, v(56.06, 49.58) * mm]});
            skFitSpline(sketch, "E243", {"points": [v(56.06, 49.58) * mm, v(56.65, 49.58) * mm, v(57.2, 49.55) * mm, v(57.73, 49.5) * mm]});
            skFitSpline(sketch, "E244", {"points": [v(57.73, 49.5) * mm, v(57.7, 49.87) * mm, v(57.68, 50.26) * mm, v(57.65, 50.66) * mm]});
            skFitSpline(sketch, "E245", {"points": [v(57.65, 50.66) * mm, v(57.65, 51.08) * mm, v(57.65, 51.5) * mm, v(57.65, 51.93) * mm]});
            skFitSpline(sketch, "E246", {"points": [v(57.65, 54.51) * mm, v(57.65, 55.87) * mm, v(57.68, 57.14) * mm, v(57.73, 58.33) * mm]});
            skFitSpline(sketch, "E247", {"points": [v(57.73, 58.33) * mm, v(57.79, 59.55) * mm, v(57.81, 60.74) * mm, v(57.81, 61.88) * mm]});
            skFitSpline(sketch, "E248", {"points": [v(57.81, 61.88) * mm, v(57.81, 63.25) * mm, v(57.61, 64.38) * mm, v(57.22, 65.26) * mm]});
            skFitSpline(sketch, "E249", {"points": [v(57.22, 65.26) * mm, v(56.85, 66.16) * mm, v(56.35, 66.86) * mm, v(55.74, 67.37) * mm]});
            skFitSpline(sketch, "E250", {"points": [v(55.74, 67.37) * mm, v(55.13, 67.9) * mm, v(54.44, 68.27) * mm, v(53.68, 68.48) * mm]});
            skFitSpline(sketch, "E251", {"points": [v(53.68, 68.48) * mm, v(52.93, 68.7) * mm, v(52.2, 68.8) * mm, v(51.45, 68.8) * mm]});
            skFitSpline(sketch, "E252", {"points": [v(51.45, 68.8) * mm, v(50.01, 68.8) * mm, v(48.78, 68.48) * mm, v(47.75, 67.84) * mm]});
            skFitSpline(sketch, "E253", {"points": [v(47.75, 67.84) * mm, v(46.71, 67.23) * mm, v(45.82, 66.36) * mm, v(45.08, 65.22) * mm]});
            skFitSpline(sketch, "E254", {"points": [v(45, 65.22) * mm, v(45, 66.28) * mm, v(45.04, 67.34) * mm, v(45.12, 68.4) * mm]});
            skFitSpline(sketch, "E255", {"points": [v(45.12, 68.4) * mm, v(44.78, 68.35) * mm, v(44.47, 68.3) * mm, v(44.2, 68.24) * mm]});
            skFitSpline(sketch, "E256", {"points": [v(44.2, 68.24) * mm, v(43.97, 68.22) * mm, v(43.74, 68.2) * mm, v(43.53, 68.2) * mm]});
            skFitSpline(sketch, "E257", {"points": [v(43.53, 68.2) * mm, v(43.08, 68.2) * mm, v(42.48, 68.27) * mm, v(41.74, 68.4) * mm]});
            skFitSpline(sketch, "E258", {"points": [v(41.74, 68.4) * mm, v(41.87, 67.26) * mm, v(41.95, 66.03) * mm, v(41.98, 64.7) * mm]});
            skFitSpline(sketch, "E259", {"points": [v(41.98, 64.7) * mm, v(42.03, 63.4) * mm, v(42.06, 62.15) * mm, v(42.06, 60.96) * mm]});
            skFitSpline(sketch, "E260", {"points": [v(42.06, 56.82) * mm, v(42.06, 55.63) * mm, v(42.03, 54.37) * mm, v(41.98, 53.04) * mm]});
            skFitSpline(sketch, "E261", {"points": [v(41.98, 53.04) * mm, v(41.95, 51.74) * mm, v(41.87, 50.56) * mm, v(41.74, 49.5) * mm]});
            skFitSpline(sketch, "E262", {"points": [v(41.74, 49.5) * mm, v(42.35, 49.55) * mm, v(42.95, 49.58) * mm, v(43.53, 49.58) * mm]});
            skFitSpline(sketch, "E263", {"points": [v(43.53, 49.58) * mm, v(44.11, 49.58) * mm, v(44.7, 49.55) * mm, v(45.32, 49.5) * mm]});
            skFitSpline(sketch, "E264", {"points": [v(45.32, 49.5) * mm, v(45.19, 50.56) * mm, v(45.1, 51.74) * mm, v(45.04, 53.04) * mm]});
            skFitSpline(sketch, "E265", {"points": [v(45.04, 53.04) * mm, v(45.01, 54.37) * mm, v(45, 55.63) * mm, v(45, 56.82) * mm]});
            skFitSpline(sketch, "E266", {"points": [v(45, 60.2) * mm, v(45, 62.27) * mm, v(45.43, 63.88) * mm, v(46.27, 65.02) * mm]});
            skFitSpline(sketch, "E267", {"points": [v(46.27, 65.02) * mm, v(47.15, 66.16) * mm, v(48.52, 66.73) * mm, v(50.37, 66.73) * mm]});
            skFitSpline(sketch, "E268", {"points": [v(50.37, 66.73) * mm, v(51.73, 66.73) * mm, v(52.79, 66.21) * mm, v(53.56, 65.18) * mm]});
            skFitSpline(sketch, "E269", {"points": [v(53.56, 65.18) * mm, v(54.33, 64.17) * mm, v(54.7, 62.67) * mm, v(54.7, 60.68) * mm]});
            skFitSpline(sketch, "E270", {"points": [v(-42.11, 17.14) * mm, v(-42.56, 16.4) * mm, v(-43.21, 15.75) * mm, v(-44.06, 15.2) * mm]});
            skFitSpline(sketch, "E271", {"points": [v(-44.06, 15.2) * mm, v(-44.88, 14.64) * mm, v(-45.8, 14.36) * mm, v(-46.8, 14.36) * mm]});
            skFitSpline(sketch, "E272", {"points": [v(-46.8, 14.36) * mm, v(-47.68, 14.36) * mm, v(-48.48, 14.68) * mm, v(-49.2, 15.31) * mm]});
            skFitSpline(sketch, "E273", {"points": [v(-49.2, 15.31) * mm, v(-49.91, 15.95) * mm, v(-50.27, 16.9) * mm, v(-50.27, 18.14) * mm]});
            skFitSpline(sketch, "E274", {"points": [v(-50.27, 18.14) * mm, v(-50.27, 18.88) * mm, v(-50.14, 19.49) * mm, v(-49.87, 19.97) * mm]});
            skFitSpline(sketch, "E275", {"points": [v(-49.87, 19.97) * mm, v(-49.58, 20.44) * mm, v(-49.2, 20.84) * mm, v(-48.76, 21.16) * mm]});
            skFitSpline(sketch, "E276", {"points": [v(-48.76, 21.16) * mm, v(-48.28, 21.48) * mm, v(-47.75, 21.73) * mm, v(-47.17, 21.92) * mm]});
            skFitSpline(sketch, "E277", {"points": [v(-47.17, 21.92) * mm, v(-46.56, 22.1) * mm, v(-45.95, 22.25) * mm, v(-45.34, 22.35) * mm]});
            skFitSpline(sketch, "E278", {"points": [v(-45.34, 22.35) * mm, v(-44.73, 22.49) * mm, v(-44.13, 22.6) * mm, v(-43.54, 22.71) * mm]});
            skFitSpline(sketch, "E279", {"points": [v(-43.54, 22.71) * mm, v(-42.93, 22.82) * mm, v(-42.4, 22.95) * mm, v(-41.95, 23.11) * mm]});
            skFitSpline(sketch, "E280", {"points": [v(-51.34, 28.12) * mm, v(-50.9, 28.97) * mm, v(-50.22, 29.64) * mm, v(-49.31, 30.11) * mm]});
            skFitSpline(sketch, "E281", {"points": [v(-49.31, 30.11) * mm, v(-48.39, 30.6) * mm, v(-47.4, 30.83) * mm, v(-46.33, 30.83) * mm]});
            skFitSpline(sketch, "E282", {"points": [v(-46.33, 30.83) * mm, v(-45.53, 30.83) * mm, v(-44.86, 30.68) * mm, v(-44.3, 30.4) * mm]});
            skFitSpline(sketch, "E283", {"points": [v(-44.3, 30.4) * mm, v(-43.74, 30.13) * mm, v(-43.3, 29.77) * mm, v(-42.95, 29.32) * mm]});
            skFitSpline(sketch, "E284", {"points": [v(-42.95, 29.32) * mm, v(-42.6, 28.87) * mm, v(-42.35, 28.34) * mm, v(-42.2, 27.73) * mm]});
            skFitSpline(sketch, "E285", {"points": [v(-42.2, 27.73) * mm, v(-42.03, 27.12) * mm, v(-41.95, 26.48) * mm, v(-41.95, 25.82) * mm]});
            skFitSpline(sketch, "E286", {"points": [v(-41.95, 25.82) * mm, v(-41.95, 25.42) * mm, v(-42, 25.09) * mm, v(-42.07, 24.82) * mm]});
            skFitSpline(sketch, "E287", {"points": [v(-42.07, 24.82) * mm, v(-42.15, 24.58) * mm, v(-42.4, 24.37) * mm, v(-42.79, 24.18) * mm]});
            skFitSpline(sketch, "E288", {"points": [v(-42.79, 24.18) * mm, v(-43.16, 24) * mm, v(-43.76, 23.81) * mm, v(-44.58, 23.63) * mm]});
            skFitSpline(sketch, "E289", {"points": [v(-44.58, 23.63) * mm, v(-45.37, 23.47) * mm, v(-46.49, 23.27) * mm, v(-47.92, 23.03) * mm]});
            skFitSpline(sketch, "E290", {"points": [v(-47.92, 23.03) * mm, v(-49.67, 22.74) * mm, v(-51.05, 22.16) * mm, v(-52.06, 21.28) * mm]});
            skFitSpline(sketch, "E291", {"points": [v(-52.06, 21.28) * mm, v(-53.04, 20.4) * mm, v(-53.53, 19.17) * mm, v(-53.53, 17.58) * mm]});
            skFitSpline(sketch, "E292", {"points": [v(-53.53, 17.58) * mm, v(-53.53, 16.81) * mm, v(-53.39, 16.12) * mm, v(-53.1, 15.51) * mm]});
            skFitSpline(sketch, "E293", {"points": [v(-53.1, 15.51) * mm, v(-52.78, 14.93) * mm, v(-52.38, 14.42) * mm, v(-51.9, 14) * mm]});
            skFitSpline(sketch, "E294", {"points": [v(-51.9, 14) * mm, v(-51.4, 13.57) * mm, v(-50.83, 13.27) * mm, v(-50.19, 13.08) * mm]});
            skFitSpline(sketch, "E295", {"points": [v(-50.19, 13.08) * mm, v(-49.55, 12.9) * mm, v(-48.9, 12.8) * mm, v(-48.24, 12.8) * mm]});
            skFitSpline(sketch, "E296", {"points": [v(-48.24, 12.8) * mm, v(-46.89, 12.8) * mm, v(-45.75, 13.03) * mm, v(-44.82, 13.48) * mm]});
            skFitSpline(sketch, "E297", {"points": [v(-44.82, 13.48) * mm, v(-43.89, 13.93) * mm, v(-42.95, 14.64) * mm, v(-42, 15.6) * mm]});
            skFitSpline(sketch, "E298", {"points": [v(-42, 15.6) * mm, v(-41.91, 14.9) * mm, v(-41.65, 14.33) * mm, v(-41.2, 13.88) * mm]});
            skFitSpline(sketch, "E299", {"points": [v(-41.2, 13.88) * mm, v(-40.75, 13.46) * mm, v(-40.1, 13.24) * mm, v(-39.25, 13.24) * mm]});
            skFitSpline(sketch, "E300", {"points": [v(-39.25, 13.24) * mm, v(-38.72, 13.24) * mm, v(-38.24, 13.28) * mm, v(-37.82, 13.36) * mm]});
            skFitSpline(sketch, "E301", {"points": [v(-37.82, 13.36) * mm, v(-37.36, 13.44) * mm, v(-37, 13.55) * mm, v(-36.7, 13.68) * mm]});
            skFitSpline(sketch, "E302", {"points": [v(-36.7, 14.56) * mm, v(-36.83, 14.48) * mm, v(-36.98, 14.42) * mm, v(-37.14, 14.4) * mm]});
            skFitSpline(sketch, "E303", {"points": [v(-37.14, 14.4) * mm, v(-37.27, 14.4) * mm, v(-37.4, 14.4) * mm, v(-37.54, 14.4) * mm]});
            skFitSpline(sketch, "E304", {"points": [v(-37.54, 14.4) * mm, v(-37.93, 14.4) * mm, v(-38.24, 14.49) * mm, v(-38.45, 14.68) * mm]});
            skFitSpline(sketch, "E305", {"points": [v(-38.45, 14.68) * mm, v(-38.64, 14.86) * mm, v(-38.78, 15.09) * mm, v(-38.89, 15.35) * mm]});
            skFitSpline(sketch, "E306", {"points": [v(-38.89, 15.35) * mm, v(-39, 15.64) * mm, v(-39.06, 15.96) * mm, v(-39.09, 16.3) * mm]});
            skFitSpline(sketch, "E307", {"points": [v(-39.09, 16.3) * mm, v(-39.09, 16.68) * mm, v(-39.09, 17.02) * mm, v(-39.09, 17.34) * mm]});
            skFitSpline(sketch, "E308", {"points": [v(-39.09, 17.34) * mm, v(-39.09, 19.01) * mm, v(-39.06, 20.6) * mm, v(-39, 22.08) * mm]});
            skFitSpline(sketch, "E309", {"points": [v(-39, 22.08) * mm, v(-38.96, 23.59) * mm, v(-38.93, 25.1) * mm, v(-38.93, 26.61) * mm]});
            skFitSpline(sketch, "E310", {"points": [v(-38.93, 26.61) * mm, v(-38.93, 27.49) * mm, v(-39.09, 28.28) * mm, v(-39.4, 29) * mm]});
            skFitSpline(sketch, "E311", {"points": [v(-39.4, 29) * mm, v(-39.73, 29.74) * mm, v(-40.16, 30.37) * mm, v(-40.72, 30.87) * mm]});
            skFitSpline(sketch, "E312", {"points": [v(-40.72, 30.87) * mm, v(-41.28, 31.4) * mm, v(-41.95, 31.8) * mm, v(-42.75, 32.06) * mm]});
            skFitSpline(sketch, "E313", {"points": [v(-42.75, 32.06) * mm, v(-43.54, 32.35) * mm, v(-44.42, 32.5) * mm, v(-45.37, 32.5) * mm]});
            skFitSpline(sketch, "E314", {"points": [v(-45.37, 32.5) * mm, v(-46.44, 32.5) * mm, v(-47.47, 32.34) * mm, v(-48.48, 32.02) * mm]});
            skFitSpline(sketch, "E315", {"points": [v(-48.48, 32.02) * mm, v(-49.49, 31.7) * mm, v(-50.59, 31.1) * mm, v(-51.78, 30.2) * mm]});
            skFitSpline(sketch, "E316", {"points": [v(-32.24, 36.04) * mm, v(-32.2, 35.2) * mm, v(-32.16, 34.37) * mm, v(-32.16, 33.57) * mm]});
            skFitSpline(sketch, "E317", {"points": [v(-32.16, 33.57) * mm, v(-32.14, 32.78) * mm, v(-32.11, 32.12) * mm, v(-32.08, 31.59) * mm]});
            skFitSpline(sketch, "E318", {"points": [v(-32.08, 31.59) * mm, v(-32.64, 31.59) * mm, v(-33.52, 31.62) * mm, v(-34.7, 31.7) * mm]});
            skFitSpline(sketch, "E319", {"points": [v(-34.7, 31.7) * mm, v(-34.68, 31.57) * mm, v(-34.67, 31.44) * mm, v(-34.67, 31.3) * mm]});
            skFitSpline(sketch, "E320", {"points": [v(-34.67, 31.3) * mm, v(-34.64, 31.17) * mm, v(-34.63, 31.04) * mm, v(-34.63, 30.9) * mm]});
            skFitSpline(sketch, "E321", {"points": [v(-34.63, 30.9) * mm, v(-34.63, 30.75) * mm, v(-34.64, 30.6) * mm, v(-34.67, 30.43) * mm]});
            skFitSpline(sketch, "E322", {"points": [v(-34.67, 30.43) * mm, v(-34.67, 30.3) * mm, v(-34.68, 30.15) * mm, v(-34.7, 30) * mm]});
            skFitSpline(sketch, "E323", {"points": [v(-34.7, 30) * mm, v(-34.44, 30.02) * mm, v(-34.2, 30.03) * mm, v(-33.95, 30.03) * mm]});
            skFitSpline(sketch, "E324", {"points": [v(-33.95, 30.03) * mm, v(-33.72, 30.06) * mm, v(-33.49, 30.07) * mm, v(-33.28, 30.07) * mm]});
            skFitSpline(sketch, "E325", {"points": [v(-32, 30.07) * mm, v(-32, 28.59) * mm, v(-32.02, 27.24) * mm, v(-32.04, 26.01) * mm]});
            skFitSpline(sketch, "E326", {"points": [v(-32.04, 26.01) * mm, v(-32.07, 24.82) * mm, v(-32.11, 23.72) * mm, v(-32.16, 22.71) * mm]});
            skFitSpline(sketch, "E327", {"points": [v(-32.16, 22.71) * mm, v(-32.2, 21.73) * mm, v(-32.22, 20.82) * mm, v(-32.24, 19.97) * mm]});
            skFitSpline(sketch, "E328", {"points": [v(-32.24, 19.97) * mm, v(-32.27, 19.14) * mm, v(-32.28, 18.38) * mm, v(-32.28, 17.66) * mm]});
            skFitSpline(sketch, "E329", {"points": [v(-32.28, 17.66) * mm, v(-32.28, 16.07) * mm, v(-31.89, 14.86) * mm, v(-31.09, 14.04) * mm]});
            skFitSpline(sketch, "E330", {"points": [v(-31.09, 14.04) * mm, v(-30.3, 13.22) * mm, v(-29.06, 12.8) * mm, v(-27.39, 12.8) * mm]});
            skFitSpline(sketch, "E331", {"points": [v(-27.39, 12.8) * mm, v(-26.89, 12.8) * mm, v(-26.37, 12.87) * mm, v(-25.84, 13) * mm]});
            skFitSpline(sketch, "E332", {"points": [v(-25.84, 13) * mm, v(-25.28, 13.11) * mm, v(-24.78, 13.2) * mm, v(-24.33, 13.28) * mm]});
            skFitSpline(sketch, "E333", {"points": [v(-24.33, 14.24) * mm, v(-24.6, 14.16) * mm, v(-24.9, 14.1) * mm, v(-25.28, 14.04) * mm]});
            skFitSpline(sketch, "E334", {"points": [v(-25.28, 14.04) * mm, v(-25.63, 13.99) * mm, v(-25.9, 13.96) * mm, v(-26.12, 13.96) * mm]});
            skFitSpline(sketch, "E335", {"points": [v(-26.12, 13.96) * mm, v(-26.91, 13.96) * mm, v(-27.52, 14.13) * mm, v(-27.95, 14.48) * mm]});
            skFitSpline(sketch, "E336", {"points": [v(-27.95, 14.48) * mm, v(-28.37, 14.82) * mm, v(-28.69, 15.27) * mm, v(-28.9, 15.83) * mm]});
            skFitSpline(sketch, "E337", {"points": [v(-28.9, 15.83) * mm, v(-29.11, 16.41) * mm, v(-29.25, 17.06) * mm, v(-29.3, 17.78) * mm]});
            skFitSpline(sketch, "E338", {"points": [v(-29.3, 17.78) * mm, v(-29.33, 18.5) * mm, v(-29.34, 19.22) * mm, v(-29.34, 19.97) * mm]});
            skFitSpline(sketch, "E339", {"points": [v(-29.34, 19.97) * mm, v(-29.34, 20.84) * mm, v(-29.34, 21.84) * mm, v(-29.34, 22.95) * mm]});
            skFitSpline(sketch, "E340", {"points": [v(-29.34, 22.95) * mm, v(-29.31, 24.07) * mm, v(-29.29, 25.13) * mm, v(-29.26, 26.13) * mm]});
            skFitSpline(sketch, "E341", {"points": [v(-29.26, 26.13) * mm, v(-29.23, 27.17) * mm, v(-29.2, 28.06) * mm, v(-29.18, 28.8) * mm]});
            skFitSpline(sketch, "E342", {"points": [v(-29.18, 28.8) * mm, v(-29.13, 29.54) * mm, v(-29.09, 29.97) * mm, v(-29.06, 30.07) * mm]});
            skFitSpline(sketch, "E343", {"points": [v(-27.11, 30.07) * mm, v(-26.69, 30.07) * mm, v(-26.29, 30.06) * mm, v(-25.92, 30.03) * mm]});
            skFitSpline(sketch, "E344", {"points": [v(-25.92, 30.03) * mm, v(-25.55, 30.03) * mm, v(-25.19, 30.02) * mm, v(-24.84, 30) * mm]});
            skFitSpline(sketch, "E345", {"points": [v(-24.84, 30) * mm, v(-24.87, 30.07) * mm, v(-24.88, 30.2) * mm, v(-24.88, 30.4) * mm]});
            skFitSpline(sketch, "E346", {"points": [v(-24.88, 31.23) * mm, v(-24.88, 31.44) * mm, v(-24.87, 31.59) * mm, v(-24.84, 31.66) * mm]});
            skFitSpline(sketch, "E347", {"points": [v(-24.84, 31.66) * mm, v(-25.77, 31.61) * mm, v(-26.63, 31.57) * mm, v(-27.43, 31.55) * mm]});
            skFitSpline(sketch, "E348", {"points": [v(-27.43, 31.55) * mm, v(-28.22, 31.55) * mm, v(-28.77, 31.55) * mm, v(-29.06, 31.55) * mm]});
            skFitSpline(sketch, "E349", {"points": [v(-29.06, 31.55) * mm, v(-29, 32.53) * mm, v(-28.97, 33.5) * mm, v(-28.94, 34.45) * mm]});
            skFitSpline(sketch, "E350", {"points": [v(-28.94, 34.45) * mm, v(-28.89, 35.43) * mm, v(-28.82, 36.43) * mm, v(-28.74, 37.43) * mm]});
            skFitSpline(sketch, "E351", {"points": [v(-21.25, 19.21) * mm, v(-21.25, 17.14) * mm, v(-20.67, 15.55) * mm, v(-19.5, 14.44) * mm]});
            skFitSpline(sketch, "E352", {"points": [v(-19.5, 14.44) * mm, v(-18.3, 13.35) * mm, v(-16.67, 12.8) * mm, v(-14.6, 12.8) * mm]});
            skFitSpline(sketch, "E353", {"points": [v(-14.6, 12.8) * mm, v(-13.33, 12.8) * mm, v(-12.15, 13.1) * mm, v(-11.06, 13.68) * mm]});
            skFitSpline(sketch, "E354", {"points": [v(-11.06, 13.68) * mm, v(-9.98, 14.3) * mm, v(-9.09, 15.23) * mm, v(-8.4, 16.5) * mm]});
            skFitSpline(sketch, "E355", {"points": [v(-8.32, 14.8) * mm, v(-8.32, 14.5) * mm, v(-8.33, 14.22) * mm, v(-8.36, 13.96) * mm]});
            skFitSpline(sketch, "E356", {"points": [v(-8.36, 13.96) * mm, v(-8.36, 13.7) * mm, v(-8.37, 13.44) * mm, v(-8.4, 13.2) * mm]});
            skFitSpline(sketch, "E357", {"points": [v(-8.4, 13.2) * mm, v(-7.87, 13.26) * mm, v(-7.35, 13.28) * mm, v(-6.85, 13.28) * mm]});
            skFitSpline(sketch, "E358", {"points": [v(-6.85, 13.28) * mm, v(-6.34, 13.28) * mm, v(-5.83, 13.26) * mm, v(-5.3, 13.2) * mm]});
            skFitSpline(sketch, "E359", {"points": [v(-5.3, 13.2) * mm, v(-5.35, 14.26) * mm, v(-5.39, 15.37) * mm, v(-5.41, 16.5) * mm]});
            skFitSpline(sketch, "E360", {"points": [v(-5.41, 16.5) * mm, v(-5.44, 17.65) * mm, v(-5.45, 18.81) * mm, v(-5.45, 20) * mm]});
            skFitSpline(sketch, "E361", {"points": [v(-5.45, 20) * mm, v(-5.45, 22.16) * mm, v(-5.44, 24.18) * mm, v(-5.41, 26.1) * mm]});
            skFitSpline(sketch, "E362", {"points": [v(-5.41, 26.1) * mm, v(-5.39, 28.03) * mm, v(-5.3, 30.03) * mm, v(-5.18, 32.1) * mm]});
            skFitSpline(sketch, "E363", {"points": [v(-5.18, 32.1) * mm, v(-5.44, 32.05) * mm, v(-5.7, 32) * mm, v(-5.97, 31.94) * mm]});
            skFitSpline(sketch, "E364", {"points": [v(-5.97, 31.94) * mm, v(-6.24, 31.92) * mm, v(-6.52, 31.9) * mm, v(-6.8, 31.9) * mm]});
            skFitSpline(sketch, "E365", {"points": [v(-6.8, 31.9) * mm, v(-7.1, 31.9) * mm, v(-7.38, 31.92) * mm, v(-7.64, 31.94) * mm]});
            skFitSpline(sketch, "E366", {"points": [v(-7.64, 31.94) * mm, v(-7.9, 32) * mm, v(-8.19, 32.05) * mm, v(-8.48, 32.1) * mm]});
            skFitSpline(sketch, "E367", {"points": [v(-8.48, 32.1) * mm, v(-8.45, 31.62) * mm, v(-8.44, 31.12) * mm, v(-8.44, 30.6) * mm]});
            skFitSpline(sketch, "E368", {"points": [v(-8.44, 30.6) * mm, v(-8.41, 30.06) * mm, v(-8.4, 29.5) * mm, v(-8.4, 28.92) * mm]});
            skFitSpline(sketch, "E369", {"points": [v(-8.4, 25.58) * mm, v(-8.4, 24.01) * mm, v(-8.41, 22.78) * mm, v(-8.44, 21.88) * mm]});
            skFitSpline(sketch, "E370", {"points": [v(-8.44, 21.88) * mm, v(-8.44, 20.98) * mm, v(-8.48, 20.26) * mm, v(-8.56, 19.73) * mm]});
            skFitSpline(sketch, "E371", {"points": [v(-8.56, 19.73) * mm, v(-8.61, 19.2) * mm, v(-8.7, 18.77) * mm, v(-8.8, 18.46) * mm]});
            skFitSpline(sketch, "E372", {"points": [v(-8.8, 18.46) * mm, v(-8.9, 18.14) * mm, v(-9.05, 17.75) * mm, v(-9.23, 17.3) * mm]});
            skFitSpline(sketch, "E373", {"points": [v(-9.23, 17.3) * mm, v(-9.58, 16.59) * mm, v(-10.12, 15.98) * mm, v(-10.87, 15.47) * mm]});
            skFitSpline(sketch, "E374", {"points": [v(-10.87, 15.47) * mm, v(-11.6, 15) * mm, v(-12.54, 14.75) * mm, v(-13.65, 14.75) * mm]});
            skFitSpline(sketch, "E375", {"points": [v(-13.65, 14.75) * mm, v(-14.42, 14.75) * mm, v(-15.1, 14.89) * mm, v(-15.68, 15.15) * mm]});
            skFitSpline(sketch, "E376", {"points": [v(-15.68, 15.15) * mm, v(-16.24, 15.44) * mm, v(-16.7, 15.8) * mm, v(-17.07, 16.23) * mm]});
            skFitSpline(sketch, "E377", {"points": [v(-17.07, 16.23) * mm, v(-17.42, 16.6) * mm, v(-17.7, 17.14) * mm, v(-17.95, 17.86) * mm]});
            skFitSpline(sketch, "E378", {"points": [v(-17.95, 17.86) * mm, v(-18.19, 18.6) * mm, v(-18.3, 19.66) * mm, v(-18.3, 21.04) * mm]});
            skFitSpline(sketch, "E379", {"points": [v(-18.3, 21.04) * mm, v(-18.3, 23.03) * mm, v(-18.28, 24.97) * mm, v(-18.23, 26.85) * mm]});
            skFitSpline(sketch, "E380", {"points": [v(-18.23, 26.85) * mm, v(-18.15, 28.76) * mm, v(-18.04, 30.51) * mm, v(-17.9, 32.1) * mm]});
            skFitSpline(sketch, "E381", {"points": [v(-17.9, 32.1) * mm, v(-18.57, 31.97) * mm, v(-19.11, 31.9) * mm, v(-19.54, 31.9) * mm]});
            skFitSpline(sketch, "E382", {"points": [v(-19.54, 31.9) * mm, v(-19.99, 31.9) * mm, v(-20.55, 31.97) * mm, v(-21.21, 32.1) * mm]});
            skFitSpline(sketch, "E383", {"points": [v(-21.21, 32.1) * mm, v(-21.18, 30.99) * mm, v(-21.17, 29.89) * mm, v(-21.17, 28.8) * mm]});
            skFitSpline(sketch, "E384", {"points": [v(-21.17, 28.8) * mm, v(-21.14, 27.71) * mm, v(-21.13, 26.7) * mm, v(-21.13, 25.78) * mm]});
            skFitSpline(sketch, "E385", {"points": [v(-21.13, 25.78) * mm, v(-21.13, 24.8) * mm, v(-21.16, 23.8) * mm, v(-21.21, 22.8) * mm]});
            skFitSpline(sketch, "E386", {"points": [v(-21.21, 22.8) * mm, v(-21.24, 21.81) * mm, v(-21.25, 20.62) * mm, v(-21.25, 19.21) * mm]});
            skFitSpline(sketch, "E387", {"points": [v(10.2, 29.04) * mm, v(10.2, 29.57) * mm, v(10.22, 30.15) * mm, v(10.25, 30.79) * mm]});
            skFitSpline(sketch, "E388", {"points": [v(10.25, 30.79) * mm, v(10.28, 31.45) * mm, v(10.36, 31.94) * mm, v(10.49, 32.26) * mm]});
            skFitSpline(sketch, "E389", {"points": [v(10.49, 32.26) * mm, v(10.22, 32.37) * mm, v(10, 32.43) * mm, v(9.81, 32.46) * mm]});
            skFitSpline(sketch, "E390", {"points": [v(9.81, 32.46) * mm, v(9.65, 32.49) * mm, v(9.45, 32.5) * mm, v(9.22, 32.5) * mm]});
            skFitSpline(sketch, "E391", {"points": [v(9.22, 32.5) * mm, v(7.28, 32.5) * mm, v(5.53, 31.07) * mm, v(3.96, 28.2) * mm]});
            skFitSpline(sketch, "E392", {"points": [v(3.88, 28.24) * mm, v(3.88, 28.75) * mm, v(3.88, 29.28) * mm, v(3.88, 29.83) * mm]});
            skFitSpline(sketch, "E393", {"points": [v(3.88, 29.83) * mm, v(3.91, 30.4) * mm, v(3.98, 31.15) * mm, v(4.08, 32.1) * mm]});
            skFitSpline(sketch, "E394", {"points": [v(4.08, 32.1) * mm, v(3.8, 32.05) * mm, v(3.51, 32) * mm, v(3.25, 31.94) * mm]});
            skFitSpline(sketch, "E395", {"points": [v(3.25, 31.94) * mm, v(2.98, 31.92) * mm, v(2.73, 31.9) * mm, v(2.5, 31.9) * mm]});
            skFitSpline(sketch, "E396", {"points": [v(2.5, 31.9) * mm, v(2.2, 31.9) * mm, v(1.92, 31.92) * mm, v(1.66, 31.94) * mm]});
            skFitSpline(sketch, "E397", {"points": [v(1.66, 31.94) * mm, v(1.4, 32) * mm, v(1.11, 32.05) * mm, v(0.82, 32.1) * mm]});
            skFitSpline(sketch, "E398", {"points": [v(0.82, 32.1) * mm, v(0.9, 30.35) * mm, v(0.94, 28.8) * mm, v(0.94, 27.45) * mm]});
            skFitSpline(sketch, "E399", {"points": [v(0.94, 27.45) * mm, v(0.97, 26.1) * mm, v(0.98, 24.9) * mm, v(0.98, 23.87) * mm]});
            skFitSpline(sketch, "E400", {"points": [v(0.98, 22.6) * mm, v(0.98, 20.34) * mm, v(0.97, 18.43) * mm, v(0.94, 16.86) * mm]});
            skFitSpline(sketch, "E401", {"points": [v(0.94, 16.86) * mm, v(0.94, 15.33) * mm, v(0.9, 14.1) * mm, v(0.82, 13.2) * mm]});
            skFitSpline(sketch, "E402", {"points": [v(0.82, 13.2) * mm, v(1.35, 13.26) * mm, v(1.9, 13.28) * mm, v(2.5, 13.28) * mm]});
            skFitSpline(sketch, "E403", {"points": [v(2.5, 13.28) * mm, v(3.02, 13.28) * mm, v(3.55, 13.26) * mm, v(4.08, 13.2) * mm]});
            skFitSpline(sketch, "E404", {"points": [v(4.08, 13.2) * mm, v(4, 13.79) * mm, v(3.95, 14.54) * mm, v(3.92, 15.47) * mm]});
            skFitSpline(sketch, "E405", {"points": [v(3.92, 15.47) * mm, v(3.92, 16.43) * mm, v(3.92, 17.8) * mm, v(3.92, 19.57) * mm]});
            skFitSpline(sketch, "E406", {"points": [v(3.92, 23.95) * mm, v(3.92, 24.72) * mm, v(4.02, 25.43) * mm, v(4.2, 26.1) * mm]});
            skFitSpline(sketch, "E407", {"points": [v(4.2, 26.1) * mm, v(4.39, 26.78) * mm, v(4.65, 27.37) * mm, v(5, 27.85) * mm]});
            skFitSpline(sketch, "E408", {"points": [v(5, 27.85) * mm, v(5.34, 28.35) * mm, v(5.77, 28.75) * mm, v(6.27, 29.04) * mm]});
            skFitSpline(sketch, "E409", {"points": [v(6.27, 29.04) * mm, v(6.77, 29.33) * mm, v(7.35, 29.48) * mm, v(7.98, 29.48) * mm]});
            skFitSpline(sketch, "E410", {"points": [v(7.98, 29.48) * mm, v(8.38, 29.48) * mm, v(8.76, 29.41) * mm, v(9.14, 29.28) * mm]});
            skFitSpline(sketch, "E411", {"points": [v(9.14, 29.28) * mm, v(9.53, 29.14) * mm, v(9.8, 29) * mm, v(9.93, 28.84) * mm]});
            skFitSpline(sketch, "E412", {"points": [v(15.14, 24.54) * mm, v(15.14, 23.64) * mm, v(15.13, 22.66) * mm, v(15.1, 21.6) * mm]});
            skFitSpline(sketch, "E413", {"points": [v(15.1, 21.6) * mm, v(15.1, 20.54) * mm, v(15.09, 19.49) * mm, v(15.06, 18.46) * mm]});
            skFitSpline(sketch, "E414", {"points": [v(15.06, 18.46) * mm, v(15.04, 17.42) * mm, v(15, 16.44) * mm, v(14.94, 15.51) * mm]});
            skFitSpline(sketch, "E415", {"points": [v(14.94, 15.51) * mm, v(14.92, 14.58) * mm, v(14.88, 13.81) * mm, v(14.82, 13.2) * mm]});
            skFitSpline(sketch, "E416", {"points": [v(14.82, 13.2) * mm, v(15.43, 13.26) * mm, v(16.03, 13.28) * mm, v(16.62, 13.28) * mm]});
            skFitSpline(sketch, "E417", {"points": [v(16.62, 13.28) * mm, v(17.2, 13.28) * mm, v(17.8, 13.26) * mm, v(18.4, 13.2) * mm]});
            skFitSpline(sketch, "E418", {"points": [v(18.4, 13.2) * mm, v(18.35, 13.81) * mm, v(18.3, 14.58) * mm, v(18.25, 15.51) * mm]});
            skFitSpline(sketch, "E419", {"points": [v(18.25, 15.51) * mm, v(18.22, 16.44) * mm, v(18.2, 17.42) * mm, v(18.17, 18.46) * mm]});
            skFitSpline(sketch, "E420", {"points": [v(18.17, 18.46) * mm, v(18.14, 19.49) * mm, v(18.11, 20.54) * mm, v(18.09, 21.6) * mm]});
            skFitSpline(sketch, "E421", {"points": [v(18.09, 21.6) * mm, v(18.09, 22.66) * mm, v(18.09, 23.64) * mm, v(18.09, 24.54) * mm]});
            skFitSpline(sketch, "E422", {"points": [v(18.09, 31.74) * mm, v(18.09, 32.65) * mm, v(18.09, 33.63) * mm, v(18.09, 34.69) * mm]});
            skFitSpline(sketch, "E423", {"points": [v(18.09, 34.69) * mm, v(18.11, 35.75) * mm, v(18.14, 36.8) * mm, v(18.17, 37.83) * mm]});
            skFitSpline(sketch, "E424", {"points": [v(18.17, 37.83) * mm, v(18.2, 38.87) * mm, v(18.22, 39.85) * mm, v(18.25, 40.78) * mm]});
            skFitSpline(sketch, "E425", {"points": [v(18.25, 40.78) * mm, v(18.3, 41.73) * mm, v(18.35, 42.54) * mm, v(18.4, 43.2) * mm]});
            skFitSpline(sketch, "E426", {"points": [v(18.4, 43.2) * mm, v(17.66, 43.07) * mm, v(17.07, 43) * mm, v(16.62, 43) * mm]});
            skFitSpline(sketch, "E427", {"points": [v(16.62, 43) * mm, v(16.16, 43) * mm, v(15.57, 43.07) * mm, v(14.82, 43.2) * mm]});
            skFitSpline(sketch, "E428", {"points": [v(14.82, 43.2) * mm, v(14.88, 42.54) * mm, v(14.92, 41.73) * mm, v(14.94, 40.78) * mm]});
            skFitSpline(sketch, "E429", {"points": [v(14.94, 40.78) * mm, v(15, 39.85) * mm, v(15.04, 38.87) * mm, v(15.06, 37.83) * mm]});
            skFitSpline(sketch, "E430", {"points": [v(15.06, 37.83) * mm, v(15.09, 36.8) * mm, v(15.1, 35.75) * mm, v(15.1, 34.69) * mm]});
            skFitSpline(sketch, "E431", {"points": [v(15.1, 34.69) * mm, v(15.13, 33.63) * mm, v(15.14, 32.65) * mm, v(15.14, 31.74) * mm]});
            skFitSpline(sketch, "E432", {"points": [v(25.7, 39.03) * mm, v(25.7, 38.47) * mm, v(25.9, 38) * mm, v(26.3, 37.6) * mm]});
            skFitSpline(sketch, "E433", {"points": [v(26.3, 37.6) * mm, v(26.7, 37.2) * mm, v(27.17, 37) * mm, v(27.73, 37) * mm]});
            skFitSpline(sketch, "E434", {"points": [v(27.73, 37) * mm, v(28.28, 37) * mm, v(28.76, 37.2) * mm, v(29.16, 37.6) * mm]});
            skFitSpline(sketch, "E435", {"points": [v(29.16, 37.6) * mm, v(29.56, 38) * mm, v(29.76, 38.47) * mm, v(29.76, 39.03) * mm]});
            skFitSpline(sketch, "E436", {"points": [v(29.76, 39.03) * mm, v(29.76, 39.58) * mm, v(29.56, 40.06) * mm, v(29.16, 40.46) * mm]});
            skFitSpline(sketch, "E437", {"points": [v(29.16, 40.46) * mm, v(28.76, 40.86) * mm, v(28.28, 41.05) * mm, v(27.73, 41.05) * mm]});
            skFitSpline(sketch, "E438", {"points": [v(27.73, 41.05) * mm, v(27.17, 41.05) * mm, v(26.7, 40.86) * mm, v(26.3, 40.46) * mm]});
            skFitSpline(sketch, "E439", {"points": [v(26.3, 40.46) * mm, v(25.9, 40.06) * mm, v(25.7, 39.58) * mm, v(25.7, 39.03) * mm]});
            skFitSpline(sketch, "E440", {"points": [v(26.26, 20.52) * mm, v(26.26, 19.33) * mm, v(26.23, 18.07) * mm, v(26.18, 16.74) * mm]});
            skFitSpline(sketch, "E441", {"points": [v(26.18, 16.74) * mm, v(26.15, 15.44) * mm, v(26.07, 14.26) * mm, v(25.94, 13.2) * mm]});
            skFitSpline(sketch, "E442", {"points": [v(25.94, 13.2) * mm, v(26.55, 13.26) * mm, v(27.14, 13.28) * mm, v(27.73, 13.28) * mm]});
            skFitSpline(sketch, "E443", {"points": [v(27.73, 13.28) * mm, v(28.31, 13.28) * mm, v(28.9, 13.26) * mm, v(29.52, 13.2) * mm]});
            skFitSpline(sketch, "E444", {"points": [v(29.52, 13.2) * mm, v(29.39, 14.26) * mm, v(29.3, 15.44) * mm, v(29.24, 16.74) * mm]});
            skFitSpline(sketch, "E445", {"points": [v(29.24, 16.74) * mm, v(29.21, 18.07) * mm, v(29.2, 19.33) * mm, v(29.2, 20.52) * mm]});
            skFitSpline(sketch, "E446", {"points": [v(29.2, 24.66) * mm, v(29.2, 25.86) * mm, v(29.21, 27.1) * mm, v(29.24, 28.4) * mm]});
            skFitSpline(sketch, "E447", {"points": [v(29.24, 28.4) * mm, v(29.3, 29.73) * mm, v(29.39, 30.96) * mm, v(29.52, 32.1) * mm]});
            skFitSpline(sketch, "E448", {"points": [v(29.52, 32.1) * mm, v(28.78, 31.97) * mm, v(28.18, 31.9) * mm, v(27.73, 31.9) * mm]});
            skFitSpline(sketch, "E449", {"points": [v(27.73, 31.9) * mm, v(27.28, 31.9) * mm, v(26.68, 31.97) * mm, v(25.94, 32.1) * mm]});
            skFitSpline(sketch, "E450", {"points": [v(25.94, 32.1) * mm, v(26.07, 30.96) * mm, v(26.15, 29.73) * mm, v(26.18, 28.4) * mm]});
            skFitSpline(sketch, "E451", {"points": [v(26.18, 28.4) * mm, v(26.23, 27.1) * mm, v(26.26, 25.86) * mm, v(26.26, 24.66) * mm]});
            skFitSpline(sketch, "E452", {"points": [v(49.35, 8.99) * mm, v(49.35, 8.08) * mm, v(49.16, 7.31) * mm, v(48.79, 6.68) * mm]});
            skFitSpline(sketch, "E453", {"points": [v(48.79, 6.68) * mm, v(48.42, 6.01) * mm, v(47.93, 5.47) * mm, v(47.32, 5.05) * mm]});
            skFitSpline(sketch, "E454", {"points": [v(47.32, 5.05) * mm, v(46.73, 4.62) * mm, v(46.06, 4.3) * mm, v(45.29, 4.1) * mm]});
            skFitSpline(sketch, "E455", {"points": [v(45.29, 4.1) * mm, v(44.52, 3.88) * mm, v(43.74, 3.77) * mm, v(42.94, 3.77) * mm]});
            skFitSpline(sketch, "E456", {"points": [v(42.94, 3.77) * mm, v(42.12, 3.77) * mm, v(41.35, 3.87) * mm, v(40.63, 4.05) * mm]});
            skFitSpline(sketch, "E457", {"points": [v(40.63, 4.05) * mm, v(39.92, 4.24) * mm, v(39.3, 4.53) * mm, v(38.76, 4.93) * mm]});
            skFitSpline(sketch, "E458", {"points": [v(38.76, 4.93) * mm, v(38.26, 5.33) * mm, v(37.85, 5.84) * mm, v(37.53, 6.48) * mm]});
            skFitSpline(sketch, "E459", {"points": [v(37.53, 6.48) * mm, v(37.24, 7.12) * mm, v(37.1, 7.88) * mm, v(37.1, 8.79) * mm]});
            skFitSpline(sketch, "E460", {"points": [v(37.1, 8.79) * mm, v(37.1, 10.48) * mm, v(37.64, 11.66) * mm, v(38.72, 12.33) * mm]});
            skFitSpline(sketch, "E461", {"points": [v(38.72, 12.33) * mm, v(39.81, 12.96) * mm, v(41.35, 13.28) * mm, v(43.34, 13.28) * mm]});
            skFitSpline(sketch, "E462", {"points": [v(43.34, 13.28) * mm, v(45.49, 13.28) * mm, v(47.03, 12.96) * mm, v(47.95, 12.33) * mm]});
            skFitSpline(sketch, "E463", {"points": [v(47.95, 12.33) * mm, v(48.88, 11.7) * mm, v(49.35, 10.58) * mm, v(49.35, 8.99) * mm]});
            skFitSpline(sketch, "E464", {"points": [v(47.2, 26.21) * mm, v(47.2, 25.47) * mm, v(47.1, 24.75) * mm, v(46.92, 24.07) * mm]});
            skFitSpline(sketch, "E465", {"points": [v(46.92, 24.07) * mm, v(46.76, 23.4) * mm, v(46.5, 22.8) * mm, v(46.12, 22.27) * mm]});
            skFitSpline(sketch, "E466", {"points": [v(46.12, 22.27) * mm, v(45.78, 21.77) * mm, v(45.33, 21.36) * mm, v(44.77, 21.04) * mm]});
            skFitSpline(sketch, "E467", {"points": [v(44.77, 21.04) * mm, v(44.24, 20.75) * mm, v(43.6, 20.6) * mm, v(42.82, 20.6) * mm]});
            skFitSpline(sketch, "E468", {"points": [v(42.82, 20.6) * mm, v(41.28, 20.6) * mm, v(40.14, 21.08) * mm, v(39.4, 22.04) * mm]});
            skFitSpline(sketch, "E469", {"points": [v(39.4, 22.04) * mm, v(38.68, 23.02) * mm, v(38.32, 24.34) * mm, v(38.32, 26.01) * mm]});
            skFitSpline(sketch, "E470", {"points": [v(38.32, 26.01) * mm, v(38.32, 27.63) * mm, v(38.72, 28.92) * mm, v(39.52, 29.87) * mm]});
            skFitSpline(sketch, "E471", {"points": [v(39.52, 29.87) * mm, v(40.31, 30.86) * mm, v(41.43, 31.35) * mm, v(42.86, 31.35) * mm]});
            skFitSpline(sketch, "E472", {"points": [v(42.86, 31.35) * mm, v(44.16, 31.35) * mm, v(45.2, 30.9) * mm, v(46, 30.03) * mm]});
            skFitSpline(sketch, "E473", {"points": [v(46, 30.03) * mm, v(46.8, 29.16) * mm, v(47.2, 27.88) * mm, v(47.2, 26.21) * mm]});
            skFitSpline(sketch, "E474", {"points": [v(35.22, 26.01) * mm, v(35.22, 24.56) * mm, v(35.57, 23.34) * mm, v(36.26, 22.35) * mm]});
            skFitSpline(sketch, "E475", {"points": [v(36.26, 22.35) * mm, v(36.95, 21.4) * mm, v(37.9, 20.66) * mm, v(39.12, 20.13) * mm]});
            skFitSpline(sketch, "E476", {"points": [v(39.12, 20.05) * mm, v(38.8, 20) * mm, v(38.47, 19.87) * mm, v(38.13, 19.69) * mm]});
            skFitSpline(sketch, "E477", {"points": [v(38.13, 19.69) * mm, v(37.78, 19.5) * mm, v(37.48, 19.26) * mm, v(37.21, 18.97) * mm]});
            skFitSpline(sketch, "E478", {"points": [v(37.21, 18.97) * mm, v(36.95, 18.68) * mm, v(36.72, 18.35) * mm, v(36.53, 17.98) * mm]});
            skFitSpline(sketch, "E479", {"points": [v(36.53, 17.98) * mm, v(36.38, 17.6) * mm, v(36.3, 17.2) * mm, v(36.3, 16.74) * mm]});
            skFitSpline(sketch, "E480", {"points": [v(36.3, 16.74) * mm, v(36.3, 15.98) * mm, v(36.5, 15.31) * mm, v(36.93, 14.75) * mm]});
            skFitSpline(sketch, "E481", {"points": [v(36.93, 14.75) * mm, v(37.36, 14.2) * mm, v(37.98, 13.8) * mm, v(38.8, 13.56) * mm]});
            skFitSpline(sketch, "E482", {"points": [v(38.8, 13.48) * mm, v(38.27, 13.35) * mm, v(37.75, 13.15) * mm, v(37.25, 12.88) * mm]});
            skFitSpline(sketch, "E483", {"points": [v(37.25, 12.88) * mm, v(36.75, 12.62) * mm, v(36.3, 12.26) * mm, v(35.9, 11.81) * mm]});
            skFitSpline(sketch, "E484", {"points": [v(35.9, 11.81) * mm, v(35.5, 11.36) * mm, v(35.17, 10.84) * mm, v(34.9, 10.26) * mm]});
            skFitSpline(sketch, "E485", {"points": [v(34.9, 10.26) * mm, v(34.66, 9.68) * mm, v(34.55, 9.04) * mm, v(34.55, 8.35) * mm]});
            skFitSpline(sketch, "E486", {"points": [v(34.55, 8.35) * mm, v(34.55, 6.57) * mm, v(35.29, 5.18) * mm, v(36.77, 4.17) * mm]});
            skFitSpline(sketch, "E487", {"points": [v(36.77, 4.17) * mm, v(38.26, 3.14) * mm, v(40.29, 2.62) * mm, v(42.86, 2.62) * mm]});
            skFitSpline(sketch, "E488", {"points": [v(42.86, 2.62) * mm, v(44.53, 2.62) * mm, v(45.96, 2.87) * mm, v(47.16, 3.38) * mm]});
            skFitSpline(sketch, "E489", {"points": [v(47.16, 3.38) * mm, v(48.35, 3.88) * mm, v(49.32, 4.52) * mm, v(50.06, 5.29) * mm]});
            skFitSpline(sketch, "E490", {"points": [v(50.06, 5.29) * mm, v(50.83, 6.05) * mm, v(51.39, 6.92) * mm, v(51.73, 7.87) * mm]});
            skFitSpline(sketch, "E491", {"points": [v(51.73, 7.87) * mm, v(52.1, 8.83) * mm, v(52.3, 9.77) * mm, v(52.3, 10.7) * mm]});
            skFitSpline(sketch, "E492", {"points": [v(52.3, 10.7) * mm, v(52.3, 11.39) * mm, v(52.16, 12.02) * mm, v(51.9, 12.6) * mm]});
            skFitSpline(sketch, "E493", {"points": [v(51.9, 12.6) * mm, v(51.65, 13.19) * mm, v(51.26, 13.7) * mm, v(50.7, 14.16) * mm]});
            skFitSpline(sketch, "E494", {"points": [v(50.7, 14.16) * mm, v(50.17, 14.6) * mm, v(49.47, 14.97) * mm, v(48.6, 15.23) * mm]});
            skFitSpline(sketch, "E495", {"points": [v(48.6, 15.23) * mm, v(47.74, 15.5) * mm, v(46.7, 15.64) * mm, v(45.49, 15.67) * mm]});
            skFitSpline(sketch, "E496", {"points": [v(45.49, 15.67) * mm, v(44.74, 15.7) * mm, v(44.01, 15.7) * mm, v(43.3, 15.7) * mm]});
            skFitSpline(sketch, "E497", {"points": [v(43.3, 15.7) * mm, v(42.58, 15.74) * mm, v(41.85, 15.76) * mm, v(41.11, 15.79) * mm]});
            skFitSpline(sketch, "E498", {"points": [v(41.11, 15.79) * mm, v(40.2, 15.82) * mm, v(39.58, 15.99) * mm, v(39.24, 16.3) * mm]});
            skFitSpline(sketch, "E499", {"points": [v(39.24, 16.3) * mm, v(38.92, 16.62) * mm, v(38.76, 17.13) * mm, v(38.76, 17.82) * mm]});
            skFitSpline(sketch, "E500", {"points": [v(38.76, 17.82) * mm, v(38.76, 18.35) * mm, v(38.96, 18.79) * mm, v(39.36, 19.13) * mm]});
            skFitSpline(sketch, "E501", {"points": [v(39.36, 19.13) * mm, v(39.78, 19.48) * mm, v(40.23, 19.65) * mm, v(40.71, 19.65) * mm]});
            skFitSpline(sketch, "E502", {"points": [v(40.71, 19.65) * mm, v(41.08, 19.65) * mm, v(41.44, 19.64) * mm, v(41.79, 19.6) * mm]});
            skFitSpline(sketch, "E503", {"points": [v(41.79, 19.6) * mm, v(42.16, 19.58) * mm, v(42.53, 19.57) * mm, v(42.9, 19.57) * mm]});
            skFitSpline(sketch, "E504", {"points": [v(42.9, 19.57) * mm, v(45.16, 19.57) * mm, v(46.95, 20.13) * mm, v(48.27, 21.24) * mm]});
            skFitSpline(sketch, "E505", {"points": [v(48.27, 21.24) * mm, v(49.62, 22.38) * mm, v(50.3, 23.95) * mm, v(50.3, 25.94) * mm]});
            skFitSpline(sketch, "E506", {"points": [v(50.3, 25.94) * mm, v(50.3, 26.94) * mm, v(50.05, 27.91) * mm, v(49.55, 28.84) * mm]});
            skFitSpline(sketch, "E507", {"points": [v(49.55, 28.84) * mm, v(49.04, 29.8) * mm, v(48.38, 30.5) * mm, v(47.56, 30.95) * mm]});
            skFitSpline(sketch, "E508", {"points": [v(47.64, 31.03) * mm, v(48.35, 31) * mm, v(49.07, 30.95) * mm, v(49.78, 30.87) * mm]});
            skFitSpline(sketch, "E509", {"points": [v(49.78, 30.87) * mm, v(50.53, 30.82) * mm, v(51.28, 30.76) * mm, v(52.05, 30.7) * mm]});
            skFitSpline(sketch, "E510", {"points": [v(52.05, 30.7) * mm, v(52.03, 30.84) * mm, v(52, 30.98) * mm, v(51.97, 31.1) * mm]});
            skFitSpline(sketch, "E511", {"points": [v(51.97, 31.1) * mm, v(51.97, 31.27) * mm, v(51.97, 31.41) * mm, v(51.97, 31.55) * mm]});
            skFitSpline(sketch, "E512", {"points": [v(51.97, 31.55) * mm, v(51.97, 31.68) * mm, v(51.97, 31.81) * mm, v(51.97, 31.94) * mm]});
            skFitSpline(sketch, "E513", {"points": [v(51.97, 31.94) * mm, v(52, 32.1) * mm, v(52.03, 32.25) * mm, v(52.05, 32.38) * mm]});
            skFitSpline(sketch, "E514", {"points": [v(52.05, 32.38) * mm, v(51.39, 32.25) * mm, v(50.31, 32.18) * mm, v(48.83, 32.18) * mm]});
            skFitSpline(sketch, "E515", {"points": [v(48.83, 32.18) * mm, v(48.54, 32.18) * mm, v(48.15, 32.2) * mm, v(47.67, 32.22) * mm]});
            skFitSpline(sketch, "E516", {"points": [v(47.67, 32.22) * mm, v(47.2, 32.25) * mm, v(46.65, 32.29) * mm, v(46.04, 32.34) * mm]});
            skFitSpline(sketch, "E517", {"points": [v(46.04, 32.34) * mm, v(45.33, 32.4) * mm, v(44.73, 32.43) * mm, v(44.25, 32.46) * mm]});
            skFitSpline(sketch, "E518", {"points": [v(44.25, 32.46) * mm, v(43.8, 32.49) * mm, v(43.32, 32.5) * mm, v(42.82, 32.5) * mm]});
            skFitSpline(sketch, "E519", {"points": [v(42.82, 32.5) * mm, v(41.79, 32.5) * mm, v(40.8, 32.37) * mm, v(39.88, 32.1) * mm]});
            skFitSpline(sketch, "E520", {"points": [v(39.88, 32.1) * mm, v(38.97, 31.84) * mm, v(38.17, 31.44) * mm, v(37.45, 30.9) * mm]});
            skFitSpline(sketch, "E521", {"points": [v(37.45, 30.9) * mm, v(36.76, 30.38) * mm, v(36.22, 29.7) * mm, v(35.82, 28.88) * mm]});
            skFitSpline(sketch, "E522", {"points": [v(35.82, 28.88) * mm, v(35.42, 28.08) * mm, v(35.22, 27.13) * mm, v(35.22, 26.01) * mm]});
            skFitSpline(sketch, "E523", {"points": [v(-33.37, -16.6) * mm, v(-33.37, -18.01) * mm, v(-33.51, -19.29) * mm, v(-33.8, -20.43) * mm]});
            skFitSpline(sketch, "E524", {"points": [v(-33.8, -20.43) * mm, v(-34.1, -21.57) * mm, v(-34.5, -22.55) * mm, v(-35.04, -23.37) * mm]});
            skFitSpline(sketch, "E525", {"points": [v(-35.04, -23.37) * mm, v(-35.54, -24.2) * mm, v(-36.14, -24.83) * mm, v(-36.83, -25.28) * mm]});
            skFitSpline(sketch, "E526", {"points": [v(-36.83, -25.28) * mm, v(-37.52, -25.7) * mm, v(-38.28, -25.92) * mm, v(-39.1, -25.92) * mm]});
            skFitSpline(sketch, "E527", {"points": [v(-39.1, -25.92) * mm, v(-42.97, -25.92) * mm, v(-44.9, -23.25) * mm, v(-44.9, -17.92) * mm]});
            skFitSpline(sketch, "E528", {"points": [v(-44.9, -17.92) * mm, v(-44.9, -16.27) * mm, v(-44.75, -14.9) * mm, v(-44.43, -13.78) * mm]});
            skFitSpline(sketch, "E529", {"points": [v(-44.43, -13.78) * mm, v(-44.08, -12.64) * mm, v(-43.63, -11.73) * mm, v(-43.08, -11.04) * mm]});
            skFitSpline(sketch, "E530", {"points": [v(-43.08, -11.04) * mm, v(-42.52, -10.32) * mm, v(-41.87, -9.82) * mm, v(-41.13, -9.52) * mm]});
            skFitSpline(sketch, "E531", {"points": [v(-41.13, -9.52) * mm, v(-40.36, -9.2) * mm, v(-39.56, -9.05) * mm, v(-38.74, -9.05) * mm]});
            skFitSpline(sketch, "E532", {"points": [v(-38.74, -9.05) * mm, v(-38.05, -9.05) * mm, v(-37.39, -9.22) * mm, v(-36.75, -9.56) * mm]});
            skFitSpline(sketch, "E533", {"points": [v(-36.75, -9.56) * mm, v(-36.09, -9.88) * mm, v(-35.52, -10.36) * mm, v(-35.04, -11) * mm]});
            skFitSpline(sketch, "E534", {"points": [v(-35.04, -11) * mm, v(-34.54, -11.63) * mm, v(-34.14, -12.43) * mm, v(-33.85, -13.38) * mm]});
            skFitSpline(sketch, "E535", {"points": [v(-33.85, -13.38) * mm, v(-33.53, -14.31) * mm, v(-33.37, -15.39) * mm, v(-33.37, -16.6) * mm]});
            skFitSpline(sketch, "E536", {"points": [v(-29.87, -16.73) * mm, v(-29.87, -15.48) * mm, v(-30.04, -14.3) * mm, v(-30.38, -13.18) * mm]});
            skFitSpline(sketch, "E537", {"points": [v(-30.38, -13.18) * mm, v(-30.7, -12.04) * mm, v(-31.2, -11.05) * mm, v(-31.86, -10.2) * mm]});
            skFitSpline(sketch, "E538", {"points": [v(-31.86, -10.2) * mm, v(-32.52, -9.35) * mm, v(-33.35, -8.68) * mm, v(-34.36, -8.17) * mm]});
            skFitSpline(sketch, "E539", {"points": [v(-34.36, -8.17) * mm, v(-35.37, -7.64) * mm, v(-36.56, -7.38) * mm, v(-37.94, -7.38) * mm]});
            skFitSpline(sketch, "E540", {"points": [v(-37.94, -7.38) * mm, v(-39.38, -7.38) * mm, v(-40.64, -7.7) * mm, v(-41.72, -8.37) * mm]});
            skFitSpline(sketch, "E541", {"points": [v(-41.72, -8.37) * mm, v(-42.81, -9.03) * mm, v(-43.8, -10.08) * mm, v(-44.7, -11.51) * mm]});
            skFitSpline(sketch, "E542", {"points": [v(-44.79, -11.51) * mm, v(-44.76, -10.3) * mm, v(-44.73, -8.94) * mm, v(-44.7, -7.46) * mm]});
            skFitSpline(sketch, "E543", {"points": [v(-44.7, -7.46) * mm, v(-44.68, -5.94) * mm, v(-44.65, -4.48) * mm, v(-44.63, -3.08) * mm]});
            skFitSpline(sketch, "E544", {"points": [v(-44.63, -3.08) * mm, v(-44.6, -1.65) * mm, v(-44.56, -0.36) * mm, v(-44.5, 0.78) * mm]});
            skFitSpline(sketch, "E545", {"points": [v(-44.5, 0.78) * mm, v(-44.46, 1.95) * mm, v(-44.39, 2.8) * mm, v(-44.3, 3.33) * mm]});
            skFitSpline(sketch, "E546", {"points": [v(-44.3, 3.33) * mm, v(-44.68, 3.27) * mm, v(-45.03, 3.22) * mm, v(-45.34, 3.17) * mm]});
            skFitSpline(sketch, "E547", {"points": [v(-45.34, 3.17) * mm, v(-45.66, 3.14) * mm, v(-45.97, 3.13) * mm, v(-46.26, 3.13) * mm]});
            skFitSpline(sketch, "E548", {"points": [v(-46.26, 3.13) * mm, v(-46.71, 3.13) * mm, v(-47.3, 3.2) * mm, v(-48.05, 3.33) * mm]});
            skFitSpline(sketch, "E549", {"points": [v(-48.05, 3.33) * mm, v(-48, 2.66) * mm, v(-47.96, 1.86) * mm, v(-47.93, 0.9) * mm]});
            skFitSpline(sketch, "E550", {"points": [v(-47.93, 0.9) * mm, v(-47.88, -0.03) * mm, v(-47.84, -1) * mm, v(-47.81, -2.04) * mm]});
            skFitSpline(sketch, "E551", {"points": [v(-47.81, -2.04) * mm, v(-47.78, -3.08) * mm, v(-47.77, -4.13) * mm, v(-47.77, -5.19) * mm]});
            skFitSpline(sketch, "E552", {"points": [v(-47.77, -5.19) * mm, v(-47.74, -6.25) * mm, v(-47.73, -7.23) * mm, v(-47.73, -8.13) * mm]});
            skFitSpline(sketch, "E553", {"points": [v(-47.73, -15.33) * mm, v(-47.73, -16.24) * mm, v(-47.74, -17.22) * mm, v(-47.77, -18.28) * mm]});
            skFitSpline(sketch, "E554", {"points": [v(-47.77, -18.28) * mm, v(-47.77, -19.34) * mm, v(-47.78, -20.39) * mm, v(-47.81, -21.42) * mm]});
            skFitSpline(sketch, "E555", {"points": [v(-47.81, -21.42) * mm, v(-47.84, -22.43) * mm, v(-47.88, -23.38) * mm, v(-47.93, -24.29) * mm]});
            skFitSpline(sketch, "E556", {"points": [v(-47.93, -24.29) * mm, v(-47.96, -25.19) * mm, v(-48, -25.96) * mm, v(-48.05, -26.6) * mm]});
            skFitSpline(sketch, "E557", {"points": [v(-47.33, -26.6) * mm, v(-46.51, -25.82) * mm, v(-45.62, -25.05) * mm, v(-44.67, -24.29) * mm]});
            skFitSpline(sketch, "E558", {"points": [v(-44.67, -24.29) * mm, v(-44.14, -25.05) * mm, v(-43.37, -25.72) * mm, v(-42.36, -26.27) * mm]});
            skFitSpline(sketch, "E559", {"points": [v(-42.36, -26.27) * mm, v(-41.33, -26.8) * mm, v(-40.17, -27.07) * mm, v(-38.9, -27.07) * mm]});
            skFitSpline(sketch, "E560", {"points": [v(-38.9, -27.07) * mm, v(-37.63, -27.07) * mm, v(-36.45, -26.83) * mm, v(-35.36, -26.35) * mm]});
            skFitSpline(sketch, "E561", {"points": [v(-35.36, -26.35) * mm, v(-34.24, -25.85) * mm, v(-33.29, -25.15) * mm, v(-32.5, -24.25) * mm]});
            skFitSpline(sketch, "E562", {"points": [v(-32.5, -24.25) * mm, v(-31.67, -23.32) * mm, v(-31.03, -22.22) * mm, v(-30.58, -20.94) * mm]});
            skFitSpline(sketch, "E563", {"points": [v(-30.58, -20.94) * mm, v(-30.1, -19.67) * mm, v(-29.87, -18.26) * mm, v(-29.87, -16.73) * mm]});
            skFitSpline(sketch, "E564", {"points": [v(-15.08, -22.73) * mm, v(-15.53, -23.48) * mm, v(-16.18, -24.13) * mm, v(-17.03, -24.68) * mm]});
            skFitSpline(sketch, "E565", {"points": [v(-17.03, -24.68) * mm, v(-17.85, -25.24) * mm, v(-18.77, -25.52) * mm, v(-19.78, -25.52) * mm]});
            skFitSpline(sketch, "E566", {"points": [v(-19.78, -25.52) * mm, v(-20.65, -25.52) * mm, v(-21.45, -25.2) * mm, v(-22.16, -24.56) * mm]});
            skFitSpline(sketch, "E567", {"points": [v(-22.16, -24.56) * mm, v(-22.88, -23.93) * mm, v(-23.24, -22.99) * mm, v(-23.24, -21.74) * mm]});
            skFitSpline(sketch, "E568", {"points": [v(-23.24, -21.74) * mm, v(-23.24, -21) * mm, v(-23.1, -20.39) * mm, v(-22.84, -19.9) * mm]});
            skFitSpline(sketch, "E569", {"points": [v(-22.84, -19.9) * mm, v(-22.55, -19.43) * mm, v(-22.18, -19.03) * mm, v(-21.72, -18.72) * mm]});
            skFitSpline(sketch, "E570", {"points": [v(-21.72, -18.72) * mm, v(-21.25, -18.4) * mm, v(-20.72, -18.14) * mm, v(-20.13, -17.96) * mm]});
            skFitSpline(sketch, "E571", {"points": [v(-20.13, -17.96) * mm, v(-19.52, -17.77) * mm, v(-18.91, -17.63) * mm, v(-18.3, -17.52) * mm]});
            skFitSpline(sketch, "E572", {"points": [v(-18.3, -17.52) * mm, v(-17.7, -17.39) * mm, v(-17.1, -17.27) * mm, v(-16.51, -17.16) * mm]});
            skFitSpline(sketch, "E573", {"points": [v(-16.51, -17.16) * mm, v(-15.9, -17.06) * mm, v(-15.37, -16.92) * mm, v(-14.92, -16.77) * mm]});
            skFitSpline(sketch, "E574", {"points": [v(-24.31, -11.75) * mm, v(-23.86, -10.9) * mm, v(-23.18, -10.24) * mm, v(-22.28, -9.76) * mm]});
            skFitSpline(sketch, "E575", {"points": [v(-22.28, -9.76) * mm, v(-21.35, -9.29) * mm, v(-20.36, -9.05) * mm, v(-19.3, -9.05) * mm]});
            skFitSpline(sketch, "E576", {"points": [v(-19.3, -9.05) * mm, v(-18.5, -9.05) * mm, v(-17.83, -9.2) * mm, v(-17.27, -9.48) * mm]});
            skFitSpline(sketch, "E577", {"points": [v(-17.27, -9.48) * mm, v(-16.71, -9.75) * mm, v(-16.26, -10.1) * mm, v(-15.92, -10.56) * mm]});
            skFitSpline(sketch, "E578", {"points": [v(-15.92, -10.56) * mm, v(-15.57, -11) * mm, v(-15.32, -11.54) * mm, v(-15.16, -12.15) * mm]});
            skFitSpline(sketch, "E579", {"points": [v(-15.16, -12.15) * mm, v(-15, -12.76) * mm, v(-14.92, -13.4) * mm, v(-14.92, -14.06) * mm]});
            skFitSpline(sketch, "E580", {"points": [v(-14.92, -14.06) * mm, v(-14.92, -14.46) * mm, v(-14.96, -14.79) * mm, v(-15.04, -15.05) * mm]});
            skFitSpline(sketch, "E581", {"points": [v(-15.04, -15.05) * mm, v(-15.12, -15.3) * mm, v(-15.36, -15.5) * mm, v(-15.76, -15.7) * mm]});
            skFitSpline(sketch, "E582", {"points": [v(-15.76, -15.7) * mm, v(-16.13, -15.88) * mm, v(-16.72, -16.06) * mm, v(-17.55, -16.25) * mm]});
            skFitSpline(sketch, "E583", {"points": [v(-17.55, -16.25) * mm, v(-18.34, -16.4) * mm, v(-19.46, -16.6) * mm, v(-20.89, -16.85) * mm]});
            skFitSpline(sketch, "E584", {"points": [v(-20.89, -16.85) * mm, v(-22.64, -17.14) * mm, v(-24.02, -17.72) * mm, v(-25.03, -18.6) * mm]});
            skFitSpline(sketch, "E585", {"points": [v(-25.03, -18.6) * mm, v(-26, -19.47) * mm, v(-26.5, -20.7) * mm, v(-26.5, -22.3) * mm]});
            skFitSpline(sketch, "E586", {"points": [v(-26.5, -22.3) * mm, v(-26.5, -23.07) * mm, v(-26.35, -23.75) * mm, v(-26.06, -24.37) * mm]});
            skFitSpline(sketch, "E587", {"points": [v(-26.06, -24.37) * mm, v(-25.74, -24.95) * mm, v(-25.35, -25.45) * mm, v(-24.87, -25.88) * mm]});
            skFitSpline(sketch, "E588", {"points": [v(-24.87, -25.88) * mm, v(-24.36, -26.3) * mm, v(-23.8, -26.6) * mm, v(-23.16, -26.8) * mm]});
            skFitSpline(sketch, "E589", {"points": [v(-23.16, -26.8) * mm, v(-22.52, -26.98) * mm, v(-21.87, -27.07) * mm, v(-21.2, -27.07) * mm]});
            skFitSpline(sketch, "E590", {"points": [v(-21.2, -27.07) * mm, v(-19.85, -27.07) * mm, v(-18.71, -26.85) * mm, v(-17.79, -26.4) * mm]});
            skFitSpline(sketch, "E591", {"points": [v(-17.79, -26.4) * mm, v(-16.86, -25.94) * mm, v(-15.92, -25.24) * mm, v(-14.96, -24.29) * mm]});
            skFitSpline(sketch, "E592", {"points": [v(-14.96, -24.29) * mm, v(-14.88, -24.98) * mm, v(-14.62, -25.55) * mm, v(-14.16, -26) * mm]});
            skFitSpline(sketch, "E593", {"points": [v(-14.16, -26) * mm, v(-13.71, -26.42) * mm, v(-13.06, -26.63) * mm, v(-12.22, -26.63) * mm]});
            skFitSpline(sketch, "E594", {"points": [v(-12.22, -26.63) * mm, v(-11.68, -26.63) * mm, v(-11.2, -26.6) * mm, v(-10.78, -26.51) * mm]});
            skFitSpline(sketch, "E595", {"points": [v(-10.78, -26.51) * mm, v(-10.33, -26.43) * mm, v(-9.96, -26.33) * mm, v(-9.67, -26.2) * mm]});
            skFitSpline(sketch, "E596", {"points": [v(-9.67, -25.32) * mm, v(-9.8, -25.4) * mm, v(-9.95, -25.45) * mm, v(-10.1, -25.48) * mm]});
            skFitSpline(sketch, "E597", {"points": [v(-10.1, -25.48) * mm, v(-10.24, -25.48) * mm, v(-10.37, -25.48) * mm, v(-10.5, -25.48) * mm]});
            skFitSpline(sketch, "E598", {"points": [v(-10.5, -25.48) * mm, v(-10.9, -25.48) * mm, v(-11.2, -25.39) * mm, v(-11.42, -25.2) * mm]});
            skFitSpline(sketch, "E599", {"points": [v(-11.42, -25.2) * mm, v(-11.6, -25.01) * mm, v(-11.75, -24.79) * mm, v(-11.86, -24.52) * mm]});
            skFitSpline(sketch, "E600", {"points": [v(-11.86, -24.52) * mm, v(-11.96, -24.23) * mm, v(-12.03, -23.91) * mm, v(-12.06, -23.57) * mm]});
            skFitSpline(sketch, "E601", {"points": [v(-12.06, -23.57) * mm, v(-12.06, -23.2) * mm, v(-12.06, -22.85) * mm, v(-12.06, -22.53) * mm]});
            skFitSpline(sketch, "E602", {"points": [v(-12.06, -22.53) * mm, v(-12.06, -20.86) * mm, v(-12.03, -19.29) * mm, v(-11.98, -17.8) * mm]});
            skFitSpline(sketch, "E603", {"points": [v(-11.98, -17.8) * mm, v(-11.92, -16.29) * mm, v(-11.9, -14.78) * mm, v(-11.9, -13.26) * mm]});
            skFitSpline(sketch, "E604", {"points": [v(-11.9, -13.26) * mm, v(-11.9, -12.39) * mm, v(-12.06, -11.6) * mm, v(-12.37, -10.88) * mm]});
            skFitSpline(sketch, "E605", {"points": [v(-12.37, -10.88) * mm, v(-12.7, -10.13) * mm, v(-13.13, -9.51) * mm, v(-13.69, -9) * mm]});
            skFitSpline(sketch, "E606", {"points": [v(-13.69, -9) * mm, v(-14.24, -8.48) * mm, v(-14.92, -8.08) * mm, v(-15.72, -7.81) * mm]});
            skFitSpline(sketch, "E607", {"points": [v(-15.72, -7.81) * mm, v(-16.51, -7.52) * mm, v(-17.39, -7.38) * mm, v(-18.34, -7.38) * mm]});
            skFitSpline(sketch, "E608", {"points": [v(-18.34, -7.38) * mm, v(-19.4, -7.38) * mm, v(-20.44, -7.53) * mm, v(-21.45, -7.85) * mm]});
            skFitSpline(sketch, "E609", {"points": [v(-21.45, -7.85) * mm, v(-22.45, -8.17) * mm, v(-23.55, -8.78) * mm, v(-24.75, -9.68) * mm]});
            skFitSpline(sketch, "E610", {"points": [v(-4.3, -15.33) * mm, v(-4.3, -16.24) * mm, v(-4.3, -17.22) * mm, v(-4.34, -18.28) * mm]});
            skFitSpline(sketch, "E611", {"points": [v(-4.34, -18.28) * mm, v(-4.34, -19.34) * mm, v(-4.35, -20.39) * mm, v(-4.38, -21.42) * mm]});
            skFitSpline(sketch, "E612", {"points": [v(-4.38, -21.42) * mm, v(-4.4, -22.46) * mm, v(-4.44, -23.44) * mm, v(-4.5, -24.37) * mm]});
            skFitSpline(sketch, "E613", {"points": [v(-4.5, -24.37) * mm, v(-4.52, -25.3) * mm, v(-4.56, -26.06) * mm, v(-4.61, -26.67) * mm]});
            skFitSpline(sketch, "E614", {"points": [v(-4.61, -26.67) * mm, v(-4, -26.62) * mm, v(-3.4, -26.6) * mm, v(-2.82, -26.6) * mm]});
            skFitSpline(sketch, "E615", {"points": [v(-2.82, -26.6) * mm, v(-2.24, -26.6) * mm, v(-1.64, -26.62) * mm, v(-1.03, -26.67) * mm]});
            skFitSpline(sketch, "E616", {"points": [v(-1.03, -26.67) * mm, v(-1.09, -26.06) * mm, v(-1.14, -25.3) * mm, v(-1.2, -24.37) * mm]});
            skFitSpline(sketch, "E617", {"points": [v(-1.2, -24.37) * mm, v(-1.22, -23.44) * mm, v(-1.25, -22.46) * mm, v(-1.27, -21.42) * mm]});
            skFitSpline(sketch, "E618", {"points": [v(-1.27, -21.42) * mm, v(-1.3, -20.39) * mm, v(-1.32, -19.34) * mm, v(-1.35, -18.28) * mm]});
            skFitSpline(sketch, "E619", {"points": [v(-1.35, -18.28) * mm, v(-1.35, -17.22) * mm, v(-1.35, -16.24) * mm, v(-1.35, -15.33) * mm]});
            skFitSpline(sketch, "E620", {"points": [v(-1.35, -8.13) * mm, v(-1.35, -7.23) * mm, v(-1.35, -6.25) * mm, v(-1.35, -5.19) * mm]});
            skFitSpline(sketch, "E621", {"points": [v(-1.35, -5.19) * mm, v(-1.32, -4.13) * mm, v(-1.3, -3.08) * mm, v(-1.27, -2.04) * mm]});
            skFitSpline(sketch, "E622", {"points": [v(-1.27, -2.04) * mm, v(-1.25, -1) * mm, v(-1.22, -0.03) * mm, v(-1.2, 0.9) * mm]});
            skFitSpline(sketch, "E623", {"points": [v(-1.2, 0.9) * mm, v(-1.14, 1.86) * mm, v(-1.09, 2.66) * mm, v(-1.03, 3.33) * mm]});
            skFitSpline(sketch, "E624", {"points": [v(-1.03, 3.33) * mm, v(-1.78, 3.2) * mm, v(-2.37, 3.13) * mm, v(-2.82, 3.13) * mm]});
            skFitSpline(sketch, "E625", {"points": [v(-2.82, 3.13) * mm, v(-3.27, 3.13) * mm, v(-3.87, 3.2) * mm, v(-4.61, 3.33) * mm]});
            skFitSpline(sketch, "E626", {"points": [v(-4.61, 3.33) * mm, v(-4.56, 2.66) * mm, v(-4.52, 1.86) * mm, v(-4.5, 0.9) * mm]});
            skFitSpline(sketch, "E627", {"points": [v(-4.5, 0.9) * mm, v(-4.44, -0.03) * mm, v(-4.4, -1) * mm, v(-4.38, -2.04) * mm]});
            skFitSpline(sketch, "E628", {"points": [v(-4.38, -2.04) * mm, v(-4.35, -3.08) * mm, v(-4.34, -4.13) * mm, v(-4.34, -5.19) * mm]});
            skFitSpline(sketch, "E629", {"points": [v(-4.34, -5.19) * mm, v(-4.3, -6.25) * mm, v(-4.3, -7.23) * mm, v(-4.3, -8.13) * mm]});
            skFitSpline(sketch, "E630", {"points": [v(15.85, -22.73) * mm, v(15.4, -23.48) * mm, v(14.75, -24.13) * mm, v(13.9, -24.68) * mm]});
            skFitSpline(sketch, "E631", {"points": [v(13.9, -24.68) * mm, v(13.08, -25.24) * mm, v(12.16, -25.52) * mm, v(11.15, -25.52) * mm]});
            skFitSpline(sketch, "E632", {"points": [v(11.15, -25.52) * mm, v(10.28, -25.52) * mm, v(9.48, -25.2) * mm, v(8.77, -24.56) * mm]});
            skFitSpline(sketch, "E633", {"points": [v(8.77, -24.56) * mm, v(8.05, -23.93) * mm, v(7.7, -22.99) * mm, v(7.7, -21.74) * mm]});
            skFitSpline(sketch, "E634", {"points": [v(7.7, -21.74) * mm, v(7.7, -21) * mm, v(7.82, -20.39) * mm, v(8.1, -19.9) * mm]});
            skFitSpline(sketch, "E635", {"points": [v(8.1, -19.9) * mm, v(8.38, -19.43) * mm, v(8.75, -19.03) * mm, v(9.2, -18.72) * mm]});
            skFitSpline(sketch, "E636", {"points": [v(9.2, -18.72) * mm, v(9.68, -18.4) * mm, v(10.21, -18.14) * mm, v(10.8, -17.96) * mm]});
            skFitSpline(sketch, "E637", {"points": [v(10.8, -17.96) * mm, v(11.4, -17.77) * mm, v(12.02, -17.63) * mm, v(12.63, -17.52) * mm]});
            skFitSpline(sketch, "E638", {"points": [v(12.63, -17.52) * mm, v(13.24, -17.39) * mm, v(13.83, -17.27) * mm, v(14.42, -17.16) * mm]});
            skFitSpline(sketch, "E639", {"points": [v(14.42, -17.16) * mm, v(15.03, -17.06) * mm, v(15.56, -16.92) * mm, v(16, -16.77) * mm]});
            skFitSpline(sketch, "E640", {"points": [v(6.62, -11.75) * mm, v(7.07, -10.9) * mm, v(7.75, -10.24) * mm, v(8.65, -9.76) * mm]});
            skFitSpline(sketch, "E641", {"points": [v(8.65, -9.76) * mm, v(9.58, -9.29) * mm, v(10.57, -9.05) * mm, v(11.63, -9.05) * mm]});
            skFitSpline(sketch, "E642", {"points": [v(11.63, -9.05) * mm, v(12.43, -9.05) * mm, v(13.1, -9.2) * mm, v(13.66, -9.48) * mm]});
            skFitSpline(sketch, "E643", {"points": [v(13.66, -9.48) * mm, v(14.22, -9.75) * mm, v(14.67, -10.1) * mm, v(15.01, -10.56) * mm]});
            skFitSpline(sketch, "E644", {"points": [v(15.01, -10.56) * mm, v(15.36, -11) * mm, v(15.6, -11.54) * mm, v(15.77, -12.15) * mm]});
            skFitSpline(sketch, "E645", {"points": [v(15.77, -12.15) * mm, v(15.93, -12.76) * mm, v(16, -13.4) * mm, v(16, -14.06) * mm]});
            skFitSpline(sketch, "E646", {"points": [v(16, -14.06) * mm, v(16, -14.46) * mm, v(15.97, -14.79) * mm, v(15.89, -15.05) * mm]});
            skFitSpline(sketch, "E647", {"points": [v(15.89, -15.05) * mm, v(15.8, -15.3) * mm, v(15.57, -15.5) * mm, v(15.17, -15.7) * mm]});
            skFitSpline(sketch, "E648", {"points": [v(15.17, -15.7) * mm, v(14.8, -15.88) * mm, v(14.2, -16.06) * mm, v(13.38, -16.25) * mm]});
            skFitSpline(sketch, "E649", {"points": [v(13.38, -16.25) * mm, v(12.59, -16.4) * mm, v(11.47, -16.6) * mm, v(10.04, -16.85) * mm]});
            skFitSpline(sketch, "E650", {"points": [v(10.04, -16.85) * mm, v(8.29, -17.14) * mm, v(6.9, -17.72) * mm, v(5.9, -18.6) * mm]});
            skFitSpline(sketch, "E651", {"points": [v(5.9, -18.6) * mm, v(4.92, -19.47) * mm, v(4.43, -20.7) * mm, v(4.43, -22.3) * mm]});
            skFitSpline(sketch, "E652", {"points": [v(4.43, -22.3) * mm, v(4.43, -23.07) * mm, v(4.58, -23.75) * mm, v(4.87, -24.37) * mm]});
            skFitSpline(sketch, "E653", {"points": [v(4.87, -24.37) * mm, v(5.19, -24.95) * mm, v(5.58, -25.45) * mm, v(6.06, -25.88) * mm]});
            skFitSpline(sketch, "E654", {"points": [v(6.06, -25.88) * mm, v(6.56, -26.3) * mm, v(7.14, -26.6) * mm, v(7.77, -26.8) * mm]});
            skFitSpline(sketch, "E655", {"points": [v(7.77, -26.8) * mm, v(8.4, -26.98) * mm, v(9.06, -27.07) * mm, v(9.72, -27.07) * mm]});
            skFitSpline(sketch, "E656", {"points": [v(9.72, -27.07) * mm, v(11.07, -27.07) * mm, v(12.21, -26.85) * mm, v(13.14, -26.4) * mm]});
            skFitSpline(sketch, "E657", {"points": [v(13.14, -26.4) * mm, v(14.07, -25.94) * mm, v(15.01, -25.24) * mm, v(15.97, -24.29) * mm]});
            skFitSpline(sketch, "E658", {"points": [v(15.97, -24.29) * mm, v(16.05, -24.98) * mm, v(16.31, -25.55) * mm, v(16.76, -26) * mm]});
            skFitSpline(sketch, "E659", {"points": [v(16.76, -26) * mm, v(17.21, -26.42) * mm, v(17.86, -26.63) * mm, v(18.71, -26.63) * mm]});
            skFitSpline(sketch, "E660", {"points": [v(18.71, -26.63) * mm, v(19.24, -26.63) * mm, v(19.72, -26.6) * mm, v(20.15, -26.51) * mm]});
            skFitSpline(sketch, "E661", {"points": [v(20.15, -26.51) * mm, v(20.6, -26.43) * mm, v(20.97, -26.33) * mm, v(21.26, -26.2) * mm]});
            skFitSpline(sketch, "E662", {"points": [v(21.26, -25.32) * mm, v(21.13, -25.4) * mm, v(20.98, -25.45) * mm, v(20.82, -25.48) * mm]});
            skFitSpline(sketch, "E663", {"points": [v(20.82, -25.48) * mm, v(20.69, -25.48) * mm, v(20.56, -25.48) * mm, v(20.42, -25.48) * mm]});
            skFitSpline(sketch, "E664", {"points": [v(20.42, -25.48) * mm, v(20.03, -25.48) * mm, v(19.72, -25.39) * mm, v(19.5, -25.2) * mm]});
            skFitSpline(sketch, "E665", {"points": [v(19.5, -25.2) * mm, v(19.32, -25.01) * mm, v(19.18, -24.79) * mm, v(19.07, -24.52) * mm]});
            skFitSpline(sketch, "E666", {"points": [v(19.07, -24.52) * mm, v(18.97, -24.23) * mm, v(18.9, -23.91) * mm, v(18.87, -23.57) * mm]});
            skFitSpline(sketch, "E667", {"points": [v(18.87, -23.57) * mm, v(18.87, -23.2) * mm, v(18.87, -22.85) * mm, v(18.87, -22.53) * mm]});
            skFitSpline(sketch, "E668", {"points": [v(18.87, -22.53) * mm, v(18.87, -20.86) * mm, v(18.9, -19.29) * mm, v(18.95, -17.8) * mm]});
            skFitSpline(sketch, "E669", {"points": [v(18.95, -17.8) * mm, v(19, -16.29) * mm, v(19.03, -14.78) * mm, v(19.03, -13.26) * mm]});
            skFitSpline(sketch, "E670", {"points": [v(19.03, -13.26) * mm, v(19.03, -12.39) * mm, v(18.87, -11.6) * mm, v(18.55, -10.88) * mm]});
            skFitSpline(sketch, "E671", {"points": [v(18.55, -10.88) * mm, v(18.24, -10.13) * mm, v(17.8, -9.51) * mm, v(17.24, -9) * mm]});
            skFitSpline(sketch, "E672", {"points": [v(17.24, -9) * mm, v(16.68, -8.48) * mm, v(16, -8.08) * mm, v(15.21, -7.81) * mm]});
            skFitSpline(sketch, "E673", {"points": [v(15.21, -7.81) * mm, v(14.42, -7.52) * mm, v(13.54, -7.38) * mm, v(12.59, -7.38) * mm]});
            skFitSpline(sketch, "E674", {"points": [v(12.59, -7.38) * mm, v(11.53, -7.38) * mm, v(10.5, -7.53) * mm, v(9.48, -7.85) * mm]});
            skFitSpline(sketch, "E675", {"points": [v(9.48, -7.85) * mm, v(8.47, -8.17) * mm, v(7.37, -8.78) * mm, v(6.18, -9.68) * mm]});
            skFitSpline(sketch, "E676", {"points": [v(38.57, -17.92) * mm, v(38.57, -19.46) * mm, v(38.53, -20.96) * mm, v(38.45, -22.42) * mm]});
            skFitSpline(sketch, "E677", {"points": [v(38.45, -22.42) * mm, v(38.4, -23.87) * mm, v(38.34, -25.3) * mm, v(38.3, -26.67) * mm]});
            skFitSpline(sketch, "E678", {"points": [v(38.3, -26.67) * mm, v(38.82, -26.62) * mm, v(39.37, -26.6) * mm, v(39.92, -26.6) * mm]});
            skFitSpline(sketch, "E679", {"points": [v(39.92, -26.6) * mm, v(40.5, -26.6) * mm, v(41.06, -26.62) * mm, v(41.6, -26.67) * mm]});
            skFitSpline(sketch, "E680", {"points": [v(41.6, -26.67) * mm, v(41.57, -26.3) * mm, v(41.54, -25.92) * mm, v(41.51, -25.52) * mm]});
            skFitSpline(sketch, "E681", {"points": [v(41.51, -25.52) * mm, v(41.51, -25.1) * mm, v(41.51, -24.67) * mm, v(41.51, -24.25) * mm]});
            skFitSpline(sketch, "E682", {"points": [v(41.51, -21.66) * mm, v(41.51, -20.3) * mm, v(41.54, -19.03) * mm, v(41.6, -17.84) * mm]});
            skFitSpline(sketch, "E683", {"points": [v(41.6, -17.84) * mm, v(41.65, -16.62) * mm, v(41.67, -15.44) * mm, v(41.67, -14.3) * mm]});
            skFitSpline(sketch, "E684", {"points": [v(41.67, -14.3) * mm, v(41.67, -12.92) * mm, v(41.47, -11.8) * mm, v(41.08, -10.92) * mm]});
            skFitSpline(sketch, "E685", {"points": [v(41.08, -10.92) * mm, v(40.7, -10.01) * mm, v(40.21, -9.31) * mm, v(39.6, -8.8) * mm]});
            skFitSpline(sketch, "E686", {"points": [v(39.6, -8.8) * mm, v(39, -8.28) * mm, v(38.3, -7.9) * mm, v(37.53, -7.7) * mm]});
            skFitSpline(sketch, "E687", {"points": [v(37.53, -7.7) * mm, v(36.8, -7.48) * mm, v(36.05, -7.38) * mm, v(35.3, -7.38) * mm]});
            skFitSpline(sketch, "E688", {"points": [v(35.3, -7.38) * mm, v(33.87, -7.38) * mm, v(32.64, -7.7) * mm, v(31.6, -8.33) * mm]});
            skFitSpline(sketch, "E689", {"points": [v(31.6, -8.33) * mm, v(30.57, -8.94) * mm, v(29.68, -9.82) * mm, v(28.94, -10.96) * mm]});
            skFitSpline(sketch, "E690", {"points": [v(28.86, -10.96) * mm, v(28.86, -9.9) * mm, v(28.9, -8.83) * mm, v(28.98, -7.77) * mm]});
            skFitSpline(sketch, "E691", {"points": [v(28.98, -7.77) * mm, v(28.64, -7.83) * mm, v(28.33, -7.88) * mm, v(28.07, -7.93) * mm]});
            skFitSpline(sketch, "E692", {"points": [v(28.07, -7.93) * mm, v(27.83, -7.96) * mm, v(27.6, -7.97) * mm, v(27.39, -7.97) * mm]});
            skFitSpline(sketch, "E693", {"points": [v(27.39, -7.97) * mm, v(26.94, -7.97) * mm, v(26.34, -7.9) * mm, v(25.6, -7.77) * mm]});
            skFitSpline(sketch, "E694", {"points": [v(25.6, -7.77) * mm, v(25.73, -8.91) * mm, v(25.81, -10.15) * mm, v(25.84, -11.47) * mm]});
            skFitSpline(sketch, "E695", {"points": [v(25.84, -11.47) * mm, v(25.9, -12.77) * mm, v(25.92, -14.02) * mm, v(25.92, -15.21) * mm]});
            skFitSpline(sketch, "E696", {"points": [v(25.92, -19.35) * mm, v(25.92, -20.55) * mm, v(25.9, -21.8) * mm, v(25.84, -23.13) * mm]});
            skFitSpline(sketch, "E697", {"points": [v(25.84, -23.13) * mm, v(25.81, -24.43) * mm, v(25.73, -25.61) * mm, v(25.6, -26.67) * mm]});
            skFitSpline(sketch, "E698", {"points": [v(25.6, -26.67) * mm, v(26.2, -26.62) * mm, v(26.8, -26.6) * mm, v(27.39, -26.6) * mm]});
            skFitSpline(sketch, "E699", {"points": [v(27.39, -26.6) * mm, v(27.97, -26.6) * mm, v(28.57, -26.62) * mm, v(29.18, -26.67) * mm]});
            skFitSpline(sketch, "E700", {"points": [v(29.18, -26.67) * mm, v(29.05, -25.61) * mm, v(28.95, -24.43) * mm, v(28.9, -23.13) * mm]});
            skFitSpline(sketch, "E701", {"points": [v(28.9, -23.13) * mm, v(28.87, -21.8) * mm, v(28.86, -20.55) * mm, v(28.86, -19.35) * mm]});
            skFitSpline(sketch, "E702", {"points": [v(28.86, -15.97) * mm, v(28.86, -13.9) * mm, v(29.29, -12.3) * mm, v(30.13, -11.16) * mm]});
            skFitSpline(sketch, "E703", {"points": [v(30.13, -11.16) * mm, v(31, -10.01) * mm, v(32.38, -9.44) * mm, v(34.23, -9.44) * mm]});
            skFitSpline(sketch, "E704", {"points": [v(34.23, -9.44) * mm, v(35.59, -9.44) * mm, v(36.65, -9.96) * mm, v(37.42, -11) * mm]});
            skFitSpline(sketch, "E705", {"points": [v(37.42, -11) * mm, v(38.18, -12) * mm, v(38.57, -13.5) * mm, v(38.57, -15.5) * mm]});
            skFitSpline(sketch, "E706", {"points": [v(-52.86, -59.72) * mm, v(-52.86, -60.12) * mm, v(-52.96, -60.62) * mm, v(-53.14, -61.23) * mm]});
            skFitSpline(sketch, "E707", {"points": [v(-53.14, -61.23) * mm, v(-53.3, -61.81) * mm, v(-53.46, -62.28) * mm, v(-53.62, -62.62) * mm]});
            skFitSpline(sketch, "E708", {"points": [v(-53.62, -62.62) * mm, v(-53.06, -62.94) * mm, v(-52.37, -63.22) * mm, v(-51.55, -63.46) * mm]});
            skFitSpline(sketch, "E709", {"points": [v(-51.55, -63.46) * mm, v(-50.73, -63.7) * mm, v(-49.7, -63.82) * mm, v(-48.49, -63.82) * mm]});
            skFitSpline(sketch, "E710", {"points": [v(-48.49, -63.82) * mm, v(-47.37, -63.82) * mm, v(-46.38, -63.66) * mm, v(-45.5, -63.34) * mm]});
            skFitSpline(sketch, "E711", {"points": [v(-45.5, -63.34) * mm, v(-44.63, -63) * mm, v(-43.88, -62.53) * mm, v(-43.27, -61.95) * mm]});
            skFitSpline(sketch, "E712", {"points": [v(-43.27, -61.95) * mm, v(-42.64, -61.34) * mm, v(-42.16, -60.66) * mm, v(-41.84, -59.92) * mm]});
            skFitSpline(sketch, "E713", {"points": [v(-41.84, -59.92) * mm, v(-41.5, -59.18) * mm, v(-41.32, -58.42) * mm, v(-41.32, -57.65) * mm]});
            skFitSpline(sketch, "E714", {"points": [v(-41.32, -57.65) * mm, v(-41.32, -56.54) * mm, v(-41.56, -55.66) * mm, v(-42.04, -55.02) * mm]});
            skFitSpline(sketch, "E715", {"points": [v(-42.04, -55.02) * mm, v(-42.5, -54.39) * mm, v(-43.06, -53.9) * mm, v(-43.75, -53.55) * mm]});
            skFitSpline(sketch, "E716", {"points": [v(-43.75, -53.55) * mm, v(-44.44, -53.18) * mm, v(-45.2, -52.9) * mm, v(-46.02, -52.72) * mm]});
            skFitSpline(sketch, "E717", {"points": [v(-46.02, -52.72) * mm, v(-46.84, -52.5) * mm, v(-47.6, -52.27) * mm, v(-48.29, -52) * mm]});
            skFitSpline(sketch, "E718", {"points": [v(-48.29, -52) * mm, v(-48.98, -51.73) * mm, v(-49.56, -51.38) * mm, v(-50.04, -50.93) * mm]});
            skFitSpline(sketch, "E719", {"points": [v(-50.04, -50.93) * mm, v(-50.49, -50.45) * mm, v(-50.71, -49.79) * mm, v(-50.71, -48.94) * mm]});
            skFitSpline(sketch, "E720", {"points": [v(-50.71, -48.94) * mm, v(-50.71, -48.35) * mm, v(-50.6, -47.85) * mm, v(-50.4, -47.42) * mm]});
            skFitSpline(sketch, "E721", {"points": [v(-50.4, -47.42) * mm, v(-50.18, -47) * mm, v(-49.92, -46.66) * mm, v(-49.6, -46.4) * mm]});
            skFitSpline(sketch, "E722", {"points": [v(-49.6, -46.4) * mm, v(-49.28, -46.12) * mm, v(-48.92, -45.93) * mm, v(-48.53, -45.8) * mm]});
            skFitSpline(sketch, "E723", {"points": [v(-48.53, -45.8) * mm, v(-48.13, -45.66) * mm, v(-47.73, -45.6) * mm, v(-47.33, -45.6) * mm]});
            skFitSpline(sketch, "E724", {"points": [v(-47.33, -45.6) * mm, v(-46.43, -45.6) * mm, v(-45.67, -45.85) * mm, v(-45.06, -46.35) * mm]});
            skFitSpline(sketch, "E725", {"points": [v(-45.06, -46.35) * mm, v(-44.45, -46.85) * mm, v(-44.04, -47.42) * mm, v(-43.83, -48.06) * mm]});
            skFitSpline(sketch, "E726", {"points": [v(-43.35, -48.06) * mm, v(-43.3, -47.74) * mm, v(-43.18, -47.3) * mm, v(-43, -46.7) * mm]});
            skFitSpline(sketch, "E727", {"points": [v(-43, -46.7) * mm, v(-42.8, -46.12) * mm, v(-42.61, -45.63) * mm, v(-42.4, -45.24) * mm]});
            skFitSpline(sketch, "E728", {"points": [v(-42.4, -45.24) * mm, v(-43, -45.02) * mm, v(-43.66, -44.79) * mm, v(-44.35, -44.52) * mm]});
            skFitSpline(sketch, "E729", {"points": [v(-44.35, -44.52) * mm, v(-45.01, -44.25) * mm, v(-45.83, -44.12) * mm, v(-46.82, -44.12) * mm]});
            skFitSpline(sketch, "E730", {"points": [v(-46.82, -44.12) * mm, v(-47.88, -44.12) * mm, v(-48.82, -44.28) * mm, v(-49.64, -44.6) * mm]});
            skFitSpline(sketch, "E731", {"points": [v(-49.64, -44.6) * mm, v(-50.46, -44.9) * mm, v(-51.15, -45.3) * mm, v(-51.7, -45.83) * mm]});
            skFitSpline(sketch, "E732", {"points": [v(-51.7, -45.83) * mm, v(-52.27, -46.36) * mm, v(-52.7, -47) * mm, v(-52.98, -47.74) * mm]});
            skFitSpline(sketch, "E733", {"points": [v(-52.98, -47.74) * mm, v(-53.27, -48.46) * mm, v(-53.42, -49.25) * mm, v(-53.42, -50.13) * mm]});
            skFitSpline(sketch, "E734", {"points": [v(-53.42, -50.13) * mm, v(-53.42, -51.24) * mm, v(-53.2, -52.12) * mm, v(-52.74, -52.76) * mm]});
            skFitSpline(sketch, "E735", {"points": [v(-52.74, -52.76) * mm, v(-52.27, -53.4) * mm, v(-51.68, -53.9) * mm, v(-51, -54.3) * mm]});
            skFitSpline(sketch, "E736", {"points": [v(-51, -54.3) * mm, v(-50.3, -54.68) * mm, v(-49.55, -54.97) * mm, v(-48.73, -55.18) * mm]});
            skFitSpline(sketch, "E737", {"points": [v(-48.73, -55.18) * mm, v(-47.9, -55.4) * mm, v(-47.15, -55.65) * mm, v(-46.46, -55.94) * mm]});
            skFitSpline(sketch, "E738", {"points": [v(-46.46, -55.94) * mm, v(-45.77, -56.2) * mm, v(-45.2, -56.56) * mm, v(-44.75, -57.01) * mm]});
            skFitSpline(sketch, "E739", {"points": [v(-44.75, -57.01) * mm, v(-44.27, -57.44) * mm, v(-44.03, -58.06) * mm, v(-44.03, -58.88) * mm]});
            skFitSpline(sketch, "E740", {"points": [v(-44.03, -58.88) * mm, v(-44.03, -59.47) * mm, v(-44.14, -59.98) * mm, v(-44.35, -60.44) * mm]});
            skFitSpline(sketch, "E741", {"points": [v(-44.35, -60.44) * mm, v(-44.56, -60.89) * mm, v(-44.85, -61.26) * mm, v(-45.22, -61.55) * mm]});
            skFitSpline(sketch, "E742", {"points": [v(-45.22, -61.55) * mm, v(-45.57, -61.84) * mm, v(-45.98, -62.07) * mm, v(-46.46, -62.23) * mm]});
            skFitSpline(sketch, "E743", {"points": [v(-46.46, -62.23) * mm, v(-46.9, -62.38) * mm, v(-47.39, -62.46) * mm, v(-47.89, -62.46) * mm]});
            skFitSpline(sketch, "E744", {"points": [v(-47.89, -62.46) * mm, v(-48.45, -62.46) * mm, v(-48.98, -62.37) * mm, v(-49.48, -62.19) * mm]});
            skFitSpline(sketch, "E745", {"points": [v(-49.48, -62.19) * mm, v(-49.96, -62) * mm, v(-50.4, -61.77) * mm, v(-50.8, -61.5) * mm]});
            skFitSpline(sketch, "E746", {"points": [v(-50.8, -61.5) * mm, v(-51.17, -61.22) * mm, v(-51.5, -60.91) * mm, v(-51.79, -60.6) * mm]});
            skFitSpline(sketch, "E747", {"points": [v(-51.79, -60.6) * mm, v(-52.05, -60.28) * mm, v(-52.25, -59.98) * mm, v(-52.39, -59.72) * mm]});
            skFitSpline(sketch, "E748", {"points": [v(-36.48, -61.55) * mm, v(-36.48, -62.16) * mm, v(-36.26, -62.68) * mm, v(-35.8, -63.1) * mm]});
            skFitSpline(sketch, "E749", {"points": [v(-35.8, -63.1) * mm, v(-35.36, -63.5) * mm, v(-34.83, -63.7) * mm, v(-34.22, -63.7) * mm]});
            skFitSpline(sketch, "E750", {"points": [v(-34.22, -63.7) * mm, v(-33.6, -63.7) * mm, v(-33.08, -63.5) * mm, v(-32.62, -63.1) * mm]});
            skFitSpline(sketch, "E751", {"points": [v(-32.62, -63.1) * mm, v(-32.17, -62.68) * mm, v(-31.95, -62.16) * mm, v(-31.95, -61.55) * mm]});
            skFitSpline(sketch, "E752", {"points": [v(-31.95, -61.55) * mm, v(-31.95, -60.94) * mm, v(-32.17, -60.4) * mm, v(-32.62, -59.96) * mm]});
            skFitSpline(sketch, "E753", {"points": [v(-32.62, -59.96) * mm, v(-33.08, -59.5) * mm, v(-33.6, -59.28) * mm, v(-34.22, -59.28) * mm]});
            skFitSpline(sketch, "E754", {"points": [v(-34.22, -59.28) * mm, v(-34.83, -59.28) * mm, v(-35.36, -59.5) * mm, v(-35.8, -59.96) * mm]});
            skFitSpline(sketch, "E755", {"points": [v(-35.8, -59.96) * mm, v(-36.26, -60.4) * mm, v(-36.48, -60.94) * mm, v(-36.48, -61.55) * mm]});
            skFitSpline(sketch, "E756", {"points": [v(-12.72, -54.67) * mm, v(-12.72, -56.2) * mm, v(-12.76, -57.7) * mm, v(-12.84, -59.16) * mm]});
            skFitSpline(sketch, "E757", {"points": [v(-12.84, -59.16) * mm, v(-12.89, -60.62) * mm, v(-12.94, -62.04) * mm, v(-13, -63.42) * mm]});
            skFitSpline(sketch, "E758", {"points": [v(-13, -63.42) * mm, v(-12.46, -63.37) * mm, v(-11.92, -63.34) * mm, v(-11.36, -63.34) * mm]});
            skFitSpline(sketch, "E759", {"points": [v(-11.36, -63.34) * mm, v(-10.78, -63.34) * mm, v(-10.22, -63.37) * mm, v(-9.7, -63.42) * mm]});
            skFitSpline(sketch, "E760", {"points": [v(-9.7, -63.42) * mm, v(-9.72, -63.05) * mm, v(-9.75, -62.66) * mm, v(-9.77, -62.27) * mm]});
            skFitSpline(sketch, "E761", {"points": [v(-9.77, -62.27) * mm, v(-9.77, -61.84) * mm, v(-9.77, -61.42) * mm, v(-9.77, -61) * mm]});
            skFitSpline(sketch, "E762", {"points": [v(-9.77, -58.4) * mm, v(-9.77, -57.05) * mm, v(-9.75, -55.78) * mm, v(-9.7, -54.59) * mm]});
            skFitSpline(sketch, "E763", {"points": [v(-9.7, -54.59) * mm, v(-9.64, -53.37) * mm, v(-9.61, -52.19) * mm, v(-9.61, -51.05) * mm]});
            skFitSpline(sketch, "E764", {"points": [v(-9.61, -51.05) * mm, v(-9.61, -49.67) * mm, v(-9.81, -48.54) * mm, v(-10.2, -47.66) * mm]});
            skFitSpline(sketch, "E765", {"points": [v(-10.2, -47.66) * mm, v(-10.58, -46.76) * mm, v(-11.07, -46.06) * mm, v(-11.68, -45.55) * mm]});
            skFitSpline(sketch, "E766", {"points": [v(-11.68, -45.55) * mm, v(-12.3, -45.02) * mm, v(-12.98, -44.65) * mm, v(-13.75, -44.44) * mm]});
            skFitSpline(sketch, "E767", {"points": [v(-13.75, -44.44) * mm, v(-14.5, -44.23) * mm, v(-15.24, -44.12) * mm, v(-15.98, -44.12) * mm]});
            skFitSpline(sketch, "E768", {"points": [v(-15.98, -44.12) * mm, v(-17.41, -44.12) * mm, v(-18.64, -44.44) * mm, v(-19.68, -45.08) * mm]});
            skFitSpline(sketch, "E769", {"points": [v(-19.68, -45.08) * mm, v(-20.71, -45.69) * mm, v(-21.6, -46.56) * mm, v(-22.35, -47.7) * mm]});
            skFitSpline(sketch, "E770", {"points": [v(-22.42, -47.7) * mm, v(-22.42, -46.64) * mm, v(-22.38, -45.58) * mm, v(-22.3, -44.52) * mm]});
            skFitSpline(sketch, "E771", {"points": [v(-22.3, -44.52) * mm, v(-22.65, -44.57) * mm, v(-22.96, -44.63) * mm, v(-23.22, -44.68) * mm]});
            skFitSpline(sketch, "E772", {"points": [v(-23.22, -44.68) * mm, v(-23.46, -44.7) * mm, v(-23.68, -44.72) * mm, v(-23.9, -44.72) * mm]});
            skFitSpline(sketch, "E773", {"points": [v(-23.9, -44.72) * mm, v(-24.35, -44.72) * mm, v(-24.94, -44.65) * mm, v(-25.69, -44.52) * mm]});
            skFitSpline(sketch, "E774", {"points": [v(-25.69, -44.52) * mm, v(-25.55, -45.66) * mm, v(-25.48, -46.9) * mm, v(-25.45, -48.22) * mm]});
            skFitSpline(sketch, "E775", {"points": [v(-25.45, -48.22) * mm, v(-25.4, -49.52) * mm, v(-25.37, -50.77) * mm, v(-25.37, -51.96) * mm]});
            skFitSpline(sketch, "E776", {"points": [v(-25.37, -56.1) * mm, v(-25.37, -57.3) * mm, v(-25.4, -58.55) * mm, v(-25.45, -59.88) * mm]});
            skFitSpline(sketch, "E777", {"points": [v(-25.45, -59.88) * mm, v(-25.48, -61.18) * mm, v(-25.55, -62.36) * mm, v(-25.69, -63.42) * mm]});
            skFitSpline(sketch, "E778", {"points": [v(-25.69, -63.42) * mm, v(-25.08, -63.37) * mm, v(-24.48, -63.34) * mm, v(-23.9, -63.34) * mm]});
            skFitSpline(sketch, "E779", {"points": [v(-23.9, -63.34) * mm, v(-23.31, -63.34) * mm, v(-22.72, -63.37) * mm, v(-22.1, -63.42) * mm]});
            skFitSpline(sketch, "E780", {"points": [v(-22.1, -63.42) * mm, v(-22.24, -62.36) * mm, v(-22.33, -61.18) * mm, v(-22.38, -59.88) * mm]});
            skFitSpline(sketch, "E781", {"points": [v(-22.38, -59.88) * mm, v(-22.41, -58.55) * mm, v(-22.42, -57.3) * mm, v(-22.42, -56.1) * mm]});
            skFitSpline(sketch, "E782", {"points": [v(-22.42, -52.72) * mm, v(-22.42, -50.65) * mm, v(-22, -49.04) * mm, v(-21.15, -47.9) * mm]});
            skFitSpline(sketch, "E783", {"points": [v(-21.15, -47.9) * mm, v(-20.28, -46.76) * mm, v(-18.91, -46.2) * mm, v(-17.05, -46.2) * mm]});
            skFitSpline(sketch, "E784", {"points": [v(-17.05, -46.2) * mm, v(-15.7, -46.2) * mm, v(-14.64, -46.7) * mm, v(-13.87, -47.74) * mm]});
            skFitSpline(sketch, "E785", {"points": [v(-13.87, -47.74) * mm, v(-13.1, -48.75) * mm, v(-12.72, -50.25) * mm, v(-12.72, -52.24) * mm]});
            skFitSpline(sketch, "E786", {"points": [v(-3.54, -57.41) * mm, v(-3.54, -59.48) * mm, v(-2.96, -61.07) * mm, v(-1.79, -62.19) * mm]});
            skFitSpline(sketch, "E787", {"points": [v(-1.79, -62.19) * mm, v(-0.6, -63.27) * mm, v(1.04, -63.82) * mm, v(3.1, -63.82) * mm]});
            skFitSpline(sketch, "E788", {"points": [v(3.1, -63.82) * mm, v(4.38, -63.82) * mm, v(5.56, -63.53) * mm, v(6.65, -62.94) * mm]});
            skFitSpline(sketch, "E789", {"points": [v(6.65, -62.94) * mm, v(7.73, -62.33) * mm, v(8.62, -61.4) * mm, v(9.31, -60.12) * mm]});
            skFitSpline(sketch, "E790", {"points": [v(9.4, -61.83) * mm, v(9.4, -62.12) * mm, v(9.38, -62.4) * mm, v(9.35, -62.66) * mm]});
            skFitSpline(sketch, "E791", {"points": [v(9.35, -62.66) * mm, v(9.35, -62.93) * mm, v(9.34, -63.18) * mm, v(9.31, -63.42) * mm]});
            skFitSpline(sketch, "E792", {"points": [v(9.31, -63.42) * mm, v(9.84, -63.37) * mm, v(10.36, -63.34) * mm, v(10.86, -63.34) * mm]});
            skFitSpline(sketch, "E793", {"points": [v(10.86, -63.34) * mm, v(11.37, -63.34) * mm, v(11.88, -63.37) * mm, v(12.42, -63.42) * mm]});
            skFitSpline(sketch, "E794", {"points": [v(12.42, -63.42) * mm, v(12.36, -62.36) * mm, v(12.32, -61.26) * mm, v(12.3, -60.12) * mm]});
            skFitSpline(sketch, "E795", {"points": [v(12.3, -60.12) * mm, v(12.27, -58.98) * mm, v(12.26, -57.8) * mm, v(12.26, -56.62) * mm]});
            skFitSpline(sketch, "E796", {"points": [v(12.26, -56.62) * mm, v(12.26, -54.47) * mm, v(12.27, -52.44) * mm, v(12.3, -50.53) * mm]});
            skFitSpline(sketch, "E797", {"points": [v(12.3, -50.53) * mm, v(12.32, -48.6) * mm, v(12.4, -46.59) * mm, v(12.53, -44.52) * mm]});
            skFitSpline(sketch, "E798", {"points": [v(12.53, -44.52) * mm, v(12.27, -44.57) * mm, v(12, -44.63) * mm, v(11.74, -44.68) * mm]});
            skFitSpline(sketch, "E799", {"points": [v(11.74, -44.68) * mm, v(11.47, -44.7) * mm, v(11.2, -44.72) * mm, v(10.9, -44.72) * mm]});
            skFitSpline(sketch, "E800", {"points": [v(10.9, -44.72) * mm, v(10.61, -44.72) * mm, v(10.33, -44.7) * mm, v(10.07, -44.68) * mm]});
            skFitSpline(sketch, "E801", {"points": [v(10.07, -44.68) * mm, v(9.8, -44.63) * mm, v(9.52, -44.57) * mm, v(9.23, -44.52) * mm]});
            skFitSpline(sketch, "E802", {"points": [v(9.23, -44.52) * mm, v(9.26, -45) * mm, v(9.27, -45.5) * mm, v(9.27, -46.03) * mm]});
            skFitSpline(sketch, "E803", {"points": [v(9.27, -46.03) * mm, v(9.3, -46.56) * mm, v(9.31, -47.12) * mm, v(9.31, -47.7) * mm]});
            skFitSpline(sketch, "E804", {"points": [v(9.31, -51.05) * mm, v(9.31, -52.61) * mm, v(9.3, -53.84) * mm, v(9.27, -54.75) * mm]});
            skFitSpline(sketch, "E805", {"points": [v(9.27, -54.75) * mm, v(9.27, -55.65) * mm, v(9.23, -56.36) * mm, v(9.15, -56.9) * mm]});
            skFitSpline(sketch, "E806", {"points": [v(9.15, -56.9) * mm, v(9.1, -57.42) * mm, v(9.02, -57.85) * mm, v(8.91, -58.17) * mm]});
            skFitSpline(sketch, "E807", {"points": [v(8.91, -58.17) * mm, v(8.8, -58.49) * mm, v(8.66, -58.87) * mm, v(8.48, -59.32) * mm]});
            skFitSpline(sketch, "E808", {"points": [v(8.48, -59.32) * mm, v(8.13, -60.04) * mm, v(7.59, -60.65) * mm, v(6.84, -61.15) * mm]});
            skFitSpline(sketch, "E809", {"points": [v(6.84, -61.15) * mm, v(6.1, -61.63) * mm, v(5.17, -61.87) * mm, v(4.06, -61.87) * mm]});
            skFitSpline(sketch, "E810", {"points": [v(4.06, -61.87) * mm, v(3.3, -61.87) * mm, v(2.61, -61.73) * mm, v(2.03, -61.47) * mm]});
            skFitSpline(sketch, "E811", {"points": [v(2.03, -61.47) * mm, v(1.47, -61.18) * mm, v(1, -60.82) * mm, v(0.64, -60.4) * mm]});
            skFitSpline(sketch, "E812", {"points": [v(0.64, -60.4) * mm, v(0.3, -60.02) * mm, v(0, -59.48) * mm, v(-0.24, -58.76) * mm]});
            skFitSpline(sketch, "E813", {"points": [v(-0.24, -58.76) * mm, v(-0.48, -58.02) * mm, v(-0.6, -56.96) * mm, v(-0.6, -55.58) * mm]});
            skFitSpline(sketch, "E814", {"points": [v(-0.6, -55.58) * mm, v(-0.6, -53.6) * mm, v(-0.57, -51.66) * mm, v(-0.52, -49.77) * mm]});
            skFitSpline(sketch, "E815", {"points": [v(-0.52, -49.77) * mm, v(-0.44, -47.86) * mm, v(-0.33, -46.11) * mm, v(-0.2, -44.52) * mm]});
            skFitSpline(sketch, "E816", {"points": [v(-0.2, -44.52) * mm, v(-0.86, -44.65) * mm, v(-1.4, -44.72) * mm, v(-1.83, -44.72) * mm]});
            skFitSpline(sketch, "E817", {"points": [v(-1.83, -44.72) * mm, v(-2.28, -44.72) * mm, v(-2.84, -44.65) * mm, v(-3.5, -44.52) * mm]});
            skFitSpline(sketch, "E818", {"points": [v(-3.5, -44.52) * mm, v(-3.47, -45.63) * mm, v(-3.46, -46.73) * mm, v(-3.46, -47.82) * mm]});
            skFitSpline(sketch, "E819", {"points": [v(-3.46, -47.82) * mm, v(-3.43, -48.9) * mm, v(-3.42, -49.92) * mm, v(-3.42, -50.85) * mm]});
            skFitSpline(sketch, "E820", {"points": [v(-3.42, -50.85) * mm, v(-3.42, -51.83) * mm, v(-3.45, -52.82) * mm, v(-3.5, -53.83) * mm]});
            skFitSpline(sketch, "E821", {"points": [v(-3.5, -53.83) * mm, v(-3.53, -54.81) * mm, v(-3.54, -56) * mm, v(-3.54, -57.41) * mm]});
            skFitSpline(sketch, "E822", {"points": [v(18.77, -61.55) * mm, v(18.77, -62.16) * mm, v(19, -62.68) * mm, v(19.45, -63.1) * mm]});
            skFitSpline(sketch, "E823", {"points": [v(19.45, -63.1) * mm, v(19.9, -63.5) * mm, v(20.43, -63.7) * mm, v(21.04, -63.7) * mm]});
            skFitSpline(sketch, "E824", {"points": [v(21.04, -63.7) * mm, v(21.65, -63.7) * mm, v(22.18, -63.5) * mm, v(22.63, -63.1) * mm]});
            skFitSpline(sketch, "E825", {"points": [v(22.63, -63.1) * mm, v(23.08, -62.68) * mm, v(23.3, -62.16) * mm, v(23.3, -61.55) * mm]});
            skFitSpline(sketch, "E826", {"points": [v(23.3, -61.55) * mm, v(23.3, -60.94) * mm, v(23.08, -60.4) * mm, v(22.63, -59.96) * mm]});
            skFitSpline(sketch, "E827", {"points": [v(22.63, -59.96) * mm, v(22.18, -59.5) * mm, v(21.65, -59.28) * mm, v(21.04, -59.28) * mm]});
            skFitSpline(sketch, "E828", {"points": [v(21.04, -59.28) * mm, v(20.43, -59.28) * mm, v(19.9, -59.5) * mm, v(19.45, -59.96) * mm]});
            skFitSpline(sketch, "E829", {"points": [v(19.45, -59.96) * mm, v(19, -60.4) * mm, v(18.77, -60.94) * mm, v(18.77, -61.55) * mm]});
            skFitSpline(sketch, "E830", {"points": [v(29.8, -61.55) * mm, v(29.8, -62.16) * mm, v(30.03, -62.68) * mm, v(30.48, -63.1) * mm]});
            skFitSpline(sketch, "E831", {"points": [v(30.48, -63.1) * mm, v(30.93, -63.5) * mm, v(31.46, -63.7) * mm, v(32.07, -63.7) * mm]});
            skFitSpline(sketch, "E832", {"points": [v(32.07, -63.7) * mm, v(32.68, -63.7) * mm, v(33.21, -63.5) * mm, v(33.66, -63.1) * mm]});
            skFitSpline(sketch, "E833", {"points": [v(33.66, -63.1) * mm, v(34.11, -62.68) * mm, v(34.34, -62.16) * mm, v(34.34, -61.55) * mm]});
            skFitSpline(sketch, "E834", {"points": [v(34.34, -61.55) * mm, v(34.34, -60.94) * mm, v(34.11, -60.4) * mm, v(33.66, -59.96) * mm]});
            skFitSpline(sketch, "E835", {"points": [v(33.66, -59.96) * mm, v(33.21, -59.5) * mm, v(32.68, -59.28) * mm, v(32.07, -59.28) * mm]});
            skFitSpline(sketch, "E836", {"points": [v(32.07, -59.28) * mm, v(31.46, -59.28) * mm, v(30.93, -59.5) * mm, v(30.48, -59.96) * mm]});
            skFitSpline(sketch, "E837", {"points": [v(30.48, -59.96) * mm, v(30.03, -60.4) * mm, v(29.8, -60.94) * mm, v(29.8, -61.55) * mm]});
            skFitSpline(sketch, "E838", {"points": [v(41.63, -52.08) * mm, v(41.63, -52.98) * mm, v(41.62, -53.96) * mm, v(41.6, -55.02) * mm]});
            skFitSpline(sketch, "E839", {"points": [v(41.6, -55.02) * mm, v(41.6, -56.09) * mm, v(41.58, -57.13) * mm, v(41.55, -58.17) * mm]});
            skFitSpline(sketch, "E840", {"points": [v(41.55, -58.17) * mm, v(41.53, -59.2) * mm, v(41.49, -60.18) * mm, v(41.44, -61.11) * mm]});
            skFitSpline(sketch, "E841", {"points": [v(41.44, -61.11) * mm, v(41.4, -62.04) * mm, v(41.37, -62.8) * mm, v(41.32, -63.42) * mm]});
            skFitSpline(sketch, "E842", {"points": [v(41.32, -63.42) * mm, v(41.93, -63.37) * mm, v(42.52, -63.34) * mm, v(43.1, -63.34) * mm]});
            skFitSpline(sketch, "E843", {"points": [v(43.1, -63.34) * mm, v(43.69, -63.34) * mm, v(44.29, -63.37) * mm, v(44.9, -63.42) * mm]});
            skFitSpline(sketch, "E844", {"points": [v(44.9, -63.42) * mm, v(44.84, -62.8) * mm, v(44.8, -62.04) * mm, v(44.74, -61.11) * mm]});
            skFitSpline(sketch, "E845", {"points": [v(44.74, -61.11) * mm, v(44.71, -60.18) * mm, v(44.68, -59.2) * mm, v(44.66, -58.17) * mm]});
            skFitSpline(sketch, "E846", {"points": [v(44.66, -58.17) * mm, v(44.63, -57.13) * mm, v(44.6, -56.09) * mm, v(44.58, -55.02) * mm]});
            skFitSpline(sketch, "E847", {"points": [v(44.58, -55.02) * mm, v(44.58, -53.96) * mm, v(44.58, -52.98) * mm, v(44.58, -52.08) * mm]});
            skFitSpline(sketch, "E848", {"points": [v(44.58, -44.88) * mm, v(44.58, -43.98) * mm, v(44.58, -43) * mm, v(44.58, -41.93) * mm]});
            skFitSpline(sketch, "E849", {"points": [v(44.58, -41.93) * mm, v(44.6, -40.87) * mm, v(44.63, -39.83) * mm, v(44.66, -38.8) * mm]});
            skFitSpline(sketch, "E850", {"points": [v(44.66, -38.8) * mm, v(44.68, -37.76) * mm, v(44.71, -36.77) * mm, v(44.74, -35.85) * mm]});
            skFitSpline(sketch, "E851", {"points": [v(44.74, -35.85) * mm, v(44.8, -34.9) * mm, v(44.84, -34.08) * mm, v(44.9, -33.42) * mm]});
            skFitSpline(sketch, "E852", {"points": [v(44.9, -33.42) * mm, v(44.15, -33.55) * mm, v(43.56, -33.62) * mm, v(43.1, -33.62) * mm]});
            skFitSpline(sketch, "E853", {"points": [v(43.1, -33.62) * mm, v(42.66, -33.62) * mm, v(42.06, -33.55) * mm, v(41.32, -33.42) * mm]});
            skFitSpline(sketch, "E854", {"points": [v(41.32, -33.42) * mm, v(41.37, -34.08) * mm, v(41.4, -34.9) * mm, v(41.44, -35.85) * mm]});
            skFitSpline(sketch, "E855", {"points": [v(41.44, -35.85) * mm, v(41.49, -36.77) * mm, v(41.53, -37.76) * mm, v(41.55, -38.8) * mm]});
            skFitSpline(sketch, "E856", {"points": [v(41.55, -38.8) * mm, v(41.58, -39.83) * mm, v(41.6, -40.87) * mm, v(41.6, -41.93) * mm]});
            skFitSpline(sketch, "E857", {"points": [v(41.6, -41.93) * mm, v(41.62, -43) * mm, v(41.63, -43.98) * mm, v(41.63, -44.88) * mm]});
            skFitSpline(sketch, "E858", {"points": [v(52.75, -52.08) * mm, v(52.75, -52.98) * mm, v(52.73, -53.96) * mm, v(52.7, -55.02) * mm]});
            skFitSpline(sketch, "E859", {"points": [v(52.7, -55.02) * mm, v(52.7, -56.09) * mm, v(52.7, -57.13) * mm, v(52.67, -58.17) * mm]});
            skFitSpline(sketch, "E860", {"points": [v(52.67, -58.17) * mm, v(52.64, -59.2) * mm, v(52.6, -60.18) * mm, v(52.55, -61.11) * mm]});
            skFitSpline(sketch, "E861", {"points": [v(52.55, -61.11) * mm, v(52.52, -62.04) * mm, v(52.48, -62.8) * mm, v(52.43, -63.42) * mm]});
            skFitSpline(sketch, "E862", {"points": [v(52.43, -63.42) * mm, v(53.04, -63.37) * mm, v(53.64, -63.34) * mm, v(54.22, -63.34) * mm]});
            skFitSpline(sketch, "E863", {"points": [v(54.22, -63.34) * mm, v(54.8, -63.34) * mm, v(55.4, -63.37) * mm, v(56, -63.42) * mm]});
            skFitSpline(sketch, "E864", {"points": [v(56, -63.42) * mm, v(55.96, -62.8) * mm, v(55.9, -62.04) * mm, v(55.85, -61.11) * mm]});
            skFitSpline(sketch, "E865", {"points": [v(55.85, -61.11) * mm, v(55.82, -60.18) * mm, v(55.8, -59.2) * mm, v(55.77, -58.17) * mm]});
            skFitSpline(sketch, "E866", {"points": [v(55.77, -58.17) * mm, v(55.74, -57.13) * mm, v(55.72, -56.09) * mm, v(55.7, -55.02) * mm]});
            skFitSpline(sketch, "E867", {"points": [v(55.7, -55.02) * mm, v(55.7, -53.96) * mm, v(55.7, -52.98) * mm, v(55.7, -52.08) * mm]});
            skFitSpline(sketch, "E868", {"points": [v(55.7, -44.88) * mm, v(55.7, -43.98) * mm, v(55.7, -43) * mm, v(55.7, -41.93) * mm]});
            skFitSpline(sketch, "E869", {"points": [v(55.7, -41.93) * mm, v(55.72, -40.87) * mm, v(55.74, -39.83) * mm, v(55.77, -38.8) * mm]});
            skFitSpline(sketch, "E870", {"points": [v(55.77, -38.8) * mm, v(55.8, -37.76) * mm, v(55.82, -36.77) * mm, v(55.85, -35.85) * mm]});
            skFitSpline(sketch, "E871", {"points": [v(55.85, -35.85) * mm, v(55.9, -34.9) * mm, v(55.96, -34.08) * mm, v(56, -33.42) * mm]});
            skFitSpline(sketch, "E872", {"points": [v(56, -33.42) * mm, v(55.27, -33.55) * mm, v(54.67, -33.62) * mm, v(54.22, -33.62) * mm]});
            skFitSpline(sketch, "E873", {"points": [v(54.22, -33.62) * mm, v(53.77, -33.62) * mm, v(53.17, -33.55) * mm, v(52.43, -33.42) * mm]});
            skFitSpline(sketch, "E874", {"points": [v(52.43, -33.42) * mm, v(52.48, -34.08) * mm, v(52.52, -34.9) * mm, v(52.55, -35.85) * mm]});
            skFitSpline(sketch, "E875", {"points": [v(52.55, -35.85) * mm, v(52.6, -36.77) * mm, v(52.64, -37.76) * mm, v(52.67, -38.8) * mm]});
            skFitSpline(sketch, "E876", {"points": [v(52.67, -38.8) * mm, v(52.7, -39.83) * mm, v(52.7, -40.87) * mm, v(52.7, -41.93) * mm]});
            skFitSpline(sketch, "E877", {"points": [v(52.7, -41.93) * mm, v(52.73, -43) * mm, v(52.75, -43.98) * mm, v(52.75, -44.88) * mm]});
            skSolve(sketch);
        }
        {
            var Q0;
            Q0=makeQuery(id+"F0.imprint","IMPRINT",FACE,{"disambiguationData":[TD([[makeQuery(id+"F0.imprint","IMPRINT",EDGE,{"derivedFrom":sQuery(id+"F0.wireOp",EDGE,"E118")}),1.0]])]});
            var Q1;
            Q1=makeQuery(id+"F0.imprint","IMPRINT",FACE,{"disambiguationData":[TD([[makeQuery(id+"F0.imprint","IMPRINT",EDGE,{"derivedFrom":sQuery(id+"F0.wireOp",EDGE,"E156")}),1.0]])]});
            var Q2;
            Q2=makeQuery(id+"F0.imprint","IMPRINT",FACE,{"disambiguationData":[TD([[makeQuery(id+"F0.imprint","IMPRINT",EDGE,{"derivedFrom":sQuery(id+"F0.wireOp",EDGE,"E194")}),1.0]])]});
            var Q3;
            Q3=makeQuery(id+"F0.imprint","IMPRINT",FACE,{"disambiguationData":[TD([[makeQuery(id+"F0.imprint","IMPRINT",EDGE,{"derivedFrom":sQuery(id+"F0.wireOp",EDGE,"E232")}),1.0]])]});
            var Q4;
            Q4=makeQuery(id+"F0.imprint","IMPRINT",FACE,{"disambiguationData":[TD([[makeQuery(id+"F0.imprint","IMPRINT",EDGE,{"derivedFrom":sQuery(id+"F0.wireOp",EDGE,"E1")}),-1.0]])]});
            var Q5;
            Q5=makeQuery(id+"F0.imprint","IMPRINT",FACE,{"disambiguationData":[TD([[makeQuery(id+"F0.imprint","IMPRINT",EDGE,{"derivedFrom":sQuery(id+"F0.wireOp",EDGE,"E11")}),-1.0]])]});
            var Q6;
            Q6=makeQuery(id+"F0.imprint","IMPRINT",FACE,{"disambiguationData":[TD([[makeQuery(id+"F0.imprint","IMPRINT",EDGE,{"derivedFrom":sQuery(id+"F0.wireOp",EDGE,"E18")}),-1.0]])]});
            var Q7;
            Q7=makeQuery(id+"F0.imprint","IMPRINT",FACE,{"disambiguationData":[TD([[makeQuery(id+"F0.imprint","IMPRINT",EDGE,{"derivedFrom":sQuery(id+"F0.wireOp",EDGE,"E30")}),1.0]])]});
            var Q8;
            Q8=makeQuery(id+"F0.imprint","IMPRINT",FACE,{"disambiguationData":[TD([[makeQuery(id+"F0.imprint","IMPRINT",EDGE,{"derivedFrom":sQuery(id+"F0.wireOp",EDGE,"E36")}),-1.0]])]});
            var Q9;
            Q9=makeQuery(id+"F0.imprint","IMPRINT",FACE,{"disambiguationData":[TD([[makeQuery(id+"F0.imprint","IMPRINT",EDGE,{"derivedFrom":sQuery(id+"F0.wireOp",EDGE,"E44")}),-1.0]])]});
            var Q10;
            Q10=makeQuery(id+"F0.imprint","IMPRINT",FACE,{"disambiguationData":[TD([[makeQuery(id+"F0.imprint","IMPRINT",EDGE,{"derivedFrom":sQuery(id+"F0.wireOp",EDGE,"E48")}),-1.0]])]});
            var Q11;
            Q11=makeQuery(id+"F0.imprint","IMPRINT",FACE,{"disambiguationData":[TD([[makeQuery(id+"F0.imprint","IMPRINT",EDGE,{"derivedFrom":sQuery(id+"F0.wireOp",EDGE,"E52")}),-1.0]])]});
            var Q12;
            Q12=makeQuery(id+"F0.imprint","IMPRINT",FACE,{"disambiguationData":[TD([[makeQuery(id+"F0.imprint","IMPRINT",EDGE,{"derivedFrom":sQuery(id+"F0.wireOp",EDGE,"E432")}),1.0]])]});
            var Q13;
            Q13=makeQuery(id+"F0.imprint","IMPRINT",FACE,{"disambiguationData":[TD([[makeQuery(id+"F0.imprint","IMPRINT",EDGE,{"derivedFrom":sQuery(id+"F0.wireOp",EDGE,"E58")}),-1.0]])]});
            var Q14;
            Q14=makeQuery(id+"F0.imprint","IMPRINT",FACE,{"disambiguationData":[TD([[makeQuery(id+"F0.imprint","IMPRINT",EDGE,{"derivedFrom":sQuery(id+"F0.wireOp",EDGE,"E64")}),-1.0]])]});
            var Q15;
            Q15=makeQuery(id+"F0.imprint","IMPRINT",FACE,{"disambiguationData":[TD([[makeQuery(id+"F0.imprint","IMPRINT",EDGE,{"derivedFrom":sQuery(id+"F0.wireOp",EDGE,"E71")}),-1.0]])]});
            var Q16;
            Q16=makeQuery(id+"F0.imprint","IMPRINT",FACE,{"disambiguationData":[TD([[makeQuery(id+"F0.imprint","IMPRINT",EDGE,{"derivedFrom":sQuery(id+"F0.wireOp",EDGE,"E75")}),-1.0]])]});
            var Q17;
            Q17=makeQuery(id+"F0.imprint","IMPRINT",FACE,{"disambiguationData":[TD([[makeQuery(id+"F0.imprint","IMPRINT",EDGE,{"derivedFrom":sQuery(id+"F0.wireOp",EDGE,"E82")}),-1.0]])]});
            var Q18;
            Q18=makeQuery(id+"F0.imprint","IMPRINT",FACE,{"disambiguationData":[TD([[makeQuery(id+"F0.imprint","IMPRINT",EDGE,{"derivedFrom":sQuery(id+"F0.wireOp",EDGE,"E92")}),-1.0]])]});
            var Q19;
            Q19=makeQuery(id+"F0.imprint","IMPRINT",FACE,{"disambiguationData":[TD([[makeQuery(id+"F0.imprint","IMPRINT",EDGE,{"derivedFrom":sQuery(id+"F0.wireOp",EDGE,"E748")}),1.0]])]});
            var Q20;
            Q20=makeQuery(id+"F0.imprint","IMPRINT",FACE,{"disambiguationData":[TD([[makeQuery(id+"F0.imprint","IMPRINT",EDGE,{"derivedFrom":sQuery(id+"F0.wireOp",EDGE,"E96")}),-1.0]])]});
            var Q21;
            Q21=makeQuery(id+"F0.imprint","IMPRINT",FACE,{"disambiguationData":[TD([[makeQuery(id+"F0.imprint","IMPRINT",EDGE,{"derivedFrom":sQuery(id+"F0.wireOp",EDGE,"E105")}),1.0]])]});
            var Q22;
            Q22=makeQuery(id+"F0.imprint","IMPRINT",FACE,{"disambiguationData":[TD([[makeQuery(id+"F0.imprint","IMPRINT",EDGE,{"derivedFrom":sQuery(id+"F0.wireOp",EDGE,"E822")}),1.0]])]});
            var Q23;
            Q23=makeQuery(id+"F0.imprint","IMPRINT",FACE,{"disambiguationData":[TD([[makeQuery(id+"F0.imprint","IMPRINT",EDGE,{"derivedFrom":sQuery(id+"F0.wireOp",EDGE,"E830")}),1.0]])]});
            var Q24;
            Q24=makeQuery(id+"F0.imprint","IMPRINT",FACE,{"disambiguationData":[TD([[makeQuery(id+"F0.imprint","IMPRINT",EDGE,{"derivedFrom":sQuery(id+"F0.wireOp",EDGE,"E111")}),-1.0]])]});
            var Q25;
            Q25=makeQuery(id+"F0.imprint","IMPRINT",FACE,{"disambiguationData":[TD([[makeQuery(id+"F0.imprint","IMPRINT",EDGE,{"derivedFrom":sQuery(id+"F0.wireOp",EDGE,"E115")}),-1.0]])]});
            extrude(context, id + "F1", {"entities" : qUnion([Q0, Q1, Q2, Q3, Q4, Q5, Q6, Q7, Q8, Q9, Q10, Q11, Q12, Q13, Q14, Q15, Q16, Q17, Q18, Q19, Q20, Q21, Q22, Q23, Q24, Q25]), "depth" : 2 * mm, "offsetDistance" : 25 * mm});
        }
    });
